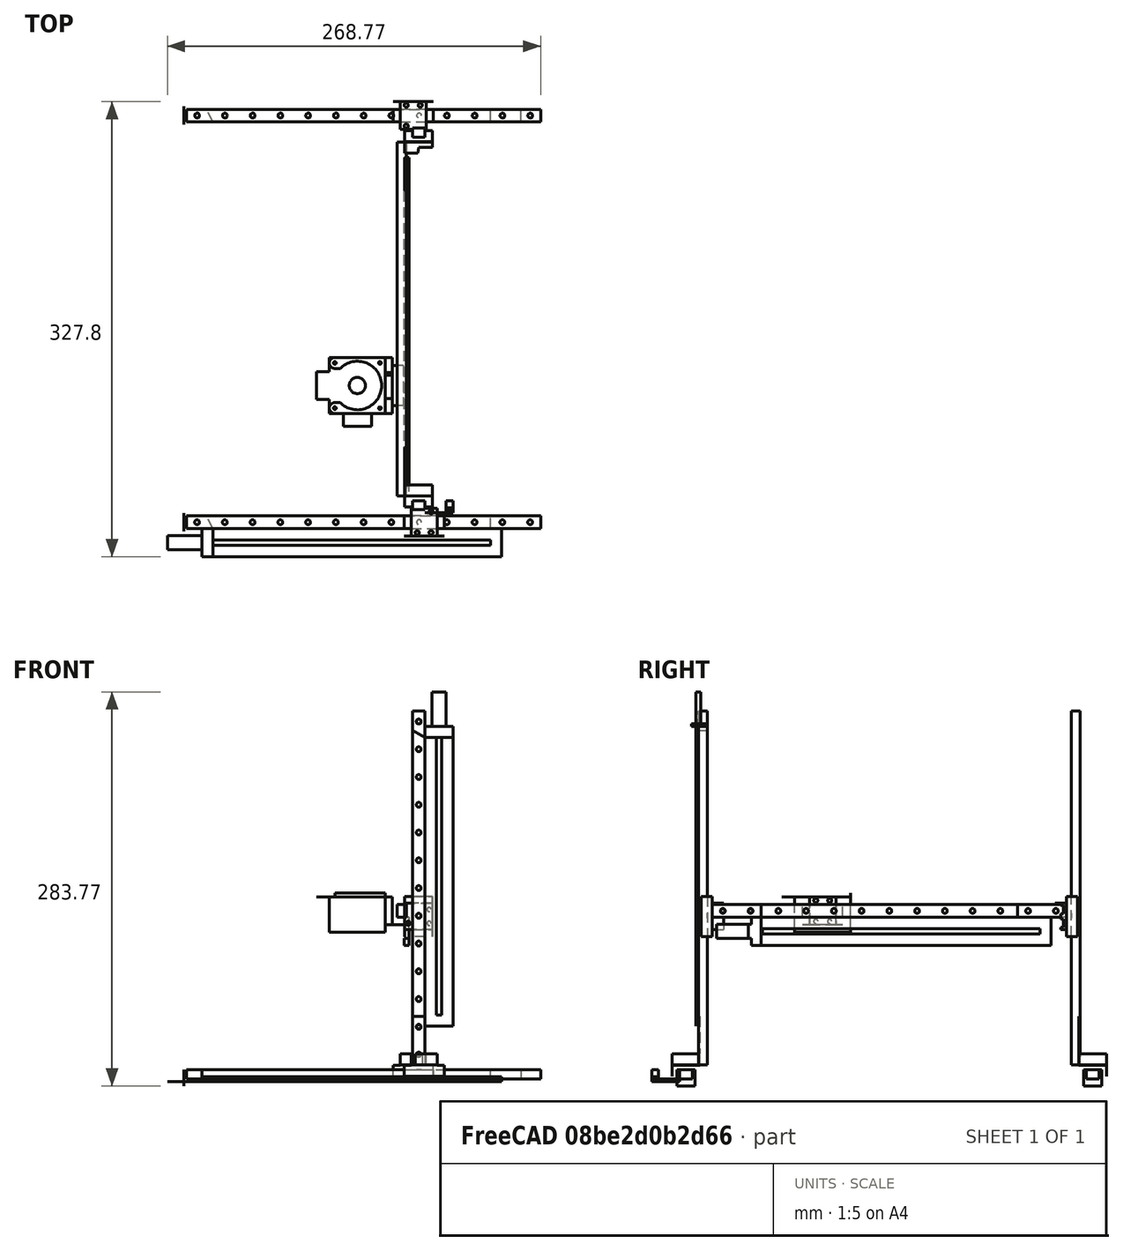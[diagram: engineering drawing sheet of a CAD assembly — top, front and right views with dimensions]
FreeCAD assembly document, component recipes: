
FREECAD ASSEMBLY — COMPONENT RECIPES ("v8")

This assembly document has 24 components, labeled P0..P23 below (a component is one placed body or linked part). 13 of them carry a construction recipe — the FreeCAD feature program that regenerates the part from scratch, quoted from this document or its linked companion documents; the rest are supplied as boundary geometry only. No exploded tour is included for this assembly.
COMPONENT P0 — geometry summary ("BaseMagentoPot"; no construction recipe available for this part):
  bounding box: 33.3 x 21.0 x 11.5 mm
  tessellated surface: 792 triangles
  volume: 2699 mm^3 (33% of its bounding box)
COMPONENT P1 — geometry summary ("Rail"; no construction recipe available for this part):
  bounding box: 255.0 x 9.0 x 6.5 mm
  tessellated surface: 3,392 triangles
  volume: 14105 mm^3 (95% of its bounding box)
  symmetry: 2-fold rotationally symmetric about the x axis; 2-fold rotationally symmetric about the y axis; 2-fold rotationally symmetric about the z axis; mirror-symmetric across its x mid-plane, y mid-plane, z mid-plane
COMPONENT P2 — recipe-attached ("Slide", a linked part whose construction recipe lives in a companion FreeCAD document of the same project; that document's serialized recipe follows).
Construction recipe (the companion document, serialized — sketch geometry with constraints, then the solid features built on it; lengths are millimeters unless a unit is written):

FCSTD DOCUMENT  (FreeCAD 0.21R33668 +26 (Git))
Label: mgn9c_slide
License: All rights reserved
LicenseURL: http://en.wikipedia.org/wiki/All_rights_reserved
objects: Sketcher::SketchObject×4, PartDesign::Pocket×3, App::Link×1, PartDesign::Pad×1, PartDesign::Body×1
note: 13 computed .brp shape members not serialized (recipe doc carries the construction recipe); baked Part::Feature solids carry a one-line shape summary decoded from their .brp
EXTERNAL_REF file=Datasheet.FCStd obj=Spreadsheet

FEATURE [App::Link] Link  label="mgn9c"
  LinkedObject = -> <external Datasheet.FCStd>#Spreadsheet
FEATURE [Sketcher::SketchObject] Sketch002
  FullyConstrained = true
  MapMode = 5
  Support = -> [XY_Plane001]
  expr: Constraints[10] = <<mgn9c>>.Dim_W
  expr: Constraints[9] = <<mgn9c>>.Dim_L
  sketch-geometry (4):
    g0: LineSegment StartX=0 StartY=0 StartZ=0 EndX=28.9 EndY=0 EndZ=0
    g1: LineSegment StartX=28.9 StartY=0 StartZ=0 EndX=28.9 EndY=20 EndZ=0
    g2: LineSegment StartX=28.9 StartY=20 StartZ=0 EndX=0 EndY=20 EndZ=0
    g3: LineSegment StartX=0 StartY=20 StartZ=0 EndX=0 EndY=0 EndZ=0
  constraints (11):
    c: Coincident(g0,g1)
    c: Coincident(g1,g2)
    c: Coincident(g2,g3)
    c: Coincident(g3,g0)
    c: Horizontal(g0)
    c: Horizontal(g2)
    c: Vertical(g1)
    c: Vertical(g3)
    c: Coincident(g0,g-1)
    c: DistanceX(g2,g2) = 28.9
    c: DistanceY(g1,g1) = 20
FEATURE [PartDesign::Pad] Pad001
  Direction = (0,0,1)
  Length = 8
  Length2 = 10
  Profile = -> Sketch002
  ReferenceAxis = -> Sketch002 [N_Axis]
  Type = 0
  expr: Length = <<mgn9c>>.Dim_H - <<mgn9c>>.Dim_H1
FEATURE [Sketcher::SketchObject] Sketch003
  ExternalGeometry = -> [Pad001]
  FullyConstrained = true
  MapMode = 5
  Placement = pos=(0,0,0) rot=(0.57735,-0.57735,-0.57735;2.0944rad)
  Support = -> [Pad001]
  expr: Constraints[10] = <<mgn9c>>.Dim_Hr - <<mgn9c>>.Dim_H1
  expr: Constraints[8] = <<mgn9c>>.Dim_N
  expr: Constraints[9] = <<mgn9c>>.Dim_N
  sketch-geometry (4):
    g0: LineSegment StartX=-14.5 StartY=0 StartZ=0 EndX=-5.5 EndY=0 EndZ=0
    g1: LineSegment StartX=-5.5 StartY=0 StartZ=0 EndX=-5.5 EndY=4.5 EndZ=0
    g2: LineSegment StartX=-5.5 StartY=4.5 StartZ=0 EndX=-14.5 EndY=4.5 EndZ=0
    g3: LineSegment StartX=-14.5 StartY=4.5 StartZ=0 EndX=-14.5 EndY=0 EndZ=0
  constraints (12):
    c: Coincident(g0,g1)
    c: Coincident(g1,g2)
    c: Coincident(g2,g3)
    c: Coincident(g3,g0)
    c: Horizontal(g0)
    c: Horizontal(g2)
    c: Vertical(g1)
    c: Vertical(g3)
    c: DistanceX(g-5,g0) = 5.5
    c: DistanceX(g0,g-6) = 5.5
    c: DistanceY(g1,g1) = 4.5
    c: PointOnObject(g0,g-5)
FEATURE [PartDesign::Pocket] Pocket001
  BaseFeature = -> Pad001
  Direction = (1,0,0)
  Length = 28.9
  Length2 = 5
  Profile = -> Sketch003
  ReferenceAxis = -> Sketch003 [N_Axis]
  Type = 0
  expr: Length = <<mgn9c>>.Dim_L
FEATURE [Sketcher::SketchObject] Sketch004
  ExternalGeometry = -> [Pocket001]
  FullyConstrained = true
  MapMode = 5
  Placement = pos=(0,0,8) rot=(0,0,1;0rad)
  Support = -> [Pocket001]
  expr: Constraints[17] = 3
  expr: Constraints[18] = 3
  expr: Constraints[19] = 3
  expr: Constraints[20] = 3
  expr: Constraints[8] = <<mgn9c>>.Dim_C
  expr: Constraints[9] = <<mgn9c>>.Dim_B
  sketch-geometry (9):
    g0: LineSegment StartX=9.45 StartY=17.5 StartZ=0 EndX=19.45 EndY=17.5 EndZ=0
    g1: LineSegment StartX=19.45 StartY=17.5 StartZ=0 EndX=19.45 EndY=2.5 EndZ=0
    g2: LineSegment StartX=19.45 StartY=2.5 StartZ=0 EndX=9.45 EndY=2.5 EndZ=0
    g3: LineSegment StartX=9.45 StartY=2.5 StartZ=0 EndX=9.45 EndY=17.5 EndZ=0
    g4: GeomPoint X=14.45 Y=10 Z=0
    g5: Circle CenterX=9.45 CenterY=17.5 CenterZ=0 NormalX=0 NormalY=0 NormalZ=1 AngleXU=0 Radius=1.5
    g6: Circle CenterX=19.45 CenterY=17.5 CenterZ=0 NormalX=0 NormalY=0 NormalZ=1 AngleXU=0 Radius=1.5
    g7: Circle CenterX=19.45 CenterY=2.5 CenterZ=0 NormalX=0 NormalY=0 NormalZ=1 AngleXU=0 Radius=1.5
    g8: Circle CenterX=9.45 CenterY=2.5 CenterZ=0 NormalX=0 NormalY=0 NormalZ=1 AngleXU=0 Radius=1.5
  constraints (21):
    c: Coincident(g0,g1)
    c: Coincident(g1,g2)
    c: Coincident(g2,g3)
    c: Coincident(g3,g0)
    c: Horizontal(g0)
    c: Horizontal(g2)
    c: Vertical(g1)
    c: Vertical(g3)
    c: DistanceX(g0,g0) = 10
    c: DistanceY(g1,g1) = 15
    c: DistanceY(g-4,g2) = 2.5
    c: Symmetric(g-3,g-4,g4)
    c: Symmetric(g1,g0,g4)
    c: Coincident(g5,g0)
    c: Coincident(g6,g0)
    c: Coincident(g7,g1)
    c: Coincident(g8,g2)
    c: Diameter(g8) = 3
    c: Diameter(g7) = 3
    c: Diameter(g6) = 3
    c: Diameter(g5) = 3
FEATURE [PartDesign::Pocket] Pocket002
  BaseFeature = -> Pocket001
  Direction = (0,0,-1)
  Length = 3
  Length2 = 5
  Profile = -> Sketch004
  ReferenceAxis = -> Sketch004 [N_Axis]
  Type = 0
FEATURE [Sketcher::SketchObject] Sketch005
  ExternalGeometry = -> [Pocket002]
  FullyConstrained = true
  MapMode = 5
  Placement = pos=(0,0,8) rot=(0,0,1;0rad)
  Support = -> [Pocket002]
  expr: Constraints[19] = <<mgn9c>>.Dim_L1
  sketch-geometry (9):
    g0: LineSegment StartX=0 StartY=20 StartZ=0 EndX=5 EndY=20 EndZ=0
    g1: LineSegment StartX=5 StartY=20 StartZ=0 EndX=5 EndY=0 EndZ=0
    g2: LineSegment StartX=5 StartY=0 StartZ=0 EndX=0 EndY=0 EndZ=0
    g3: LineSegment StartX=0 StartY=0 StartZ=0 EndX=0 EndY=20 EndZ=0
    g4: LineSegment StartX=28.9 StartY=0 StartZ=0 EndX=23.9 EndY=0 EndZ=0
    g5: LineSegment StartX=23.9 StartY=0 StartZ=0 EndX=23.9 EndY=20 EndZ=0
    g6: LineSegment StartX=23.9 StartY=20 StartZ=0 EndX=28.9 EndY=20 EndZ=0
    g7: LineSegment StartX=28.9 StartY=20 StartZ=0 EndX=28.9 EndY=0 EndZ=0
    g8: GeomPoint X=14.45 Y=0 Z=0
  constraints (22):
    c: Coincident(g0,g1)
    c: Coincident(g1,g2)
    c: Coincident(g2,g3)
    c: Coincident(g3,g0)
    c: Horizontal(g0)
    c: Horizontal(g2)
    c: Vertical(g1)
    c: Vertical(g3)
    c: Coincident(g0,g-3)
    c: PointOnObject(g1,g-1)
    c: Coincident(g4,g5)
    c: Coincident(g5,g6)
    c: Coincident(g6,g7)
    c: Coincident(g7,g4)
    c: Horizontal(g6)
    c: Vertical(g5)
    c: Vertical(g7)
    c: Symmetric(g2,g-4,g8)
    c: Symmetric(g4,g1,g8)
    c: DistanceX(g1,g4) = 18.9
    c: PointOnObject(g5,g-5)
    c: Coincident(g4,g-4)
FEATURE [PartDesign::Pocket] Pocket003
  BaseFeature = -> Pocket002
  Direction = (0,0,-1)
  Length = 0.1
  Length2 = 5
  Profile = -> Sketch005
  ReferenceAxis = -> Sketch005 [N_Axis]
  Type = 0
FEATURE [PartDesign::Body] Body001  label="Slide"
  Group = -> [Sketch002,Pad001,Sketch003,Pocket001,Sketch004,Pocket002,Sketch005,Pocket003]
  Origin = -> Origin001
  Tip = -> Pocket003
COMPONENT P3 — geometry summary ("MP1_L_0200_103_5_ST"; no construction recipe available for this part):
  bounding box: 240.7 x 20.3 x 3.5 mm
  tessellated surface: 48 triangles
  volume: 13555 mm^3 (79% of its bounding box)
  symmetry: 2-fold rotationally symmetric about the x axis; mirror-symmetric across its y mid-plane, z mid-plane
COMPONENT P4 — recipe-attached ("NormalConnectorMagnet", a linked part whose construction recipe lives in a companion FreeCAD document of the same project; that document's serialized recipe follows).
Construction recipe (the companion document, serialized — sketch geometry with constraints, then the solid features built on it; lengths are millimeters unless a unit is written):

FCSTD DOCUMENT  (FreeCAD 0.21R33668 +26 (Git))
Label: NormalConnectorMagnet
License: All rights reserved
LicenseURL: http://en.wikipedia.org/wiki/All_rights_reserved
objects: Sketcher::SketchObject×26, PartDesign::Pocket×17, PartDesign::Pad×8, PartDesign::SubShapeBinder×2, PartDesign::Body×2
note: 80 computed .brp shape members not serialized (recipe doc carries the construction recipe); baked Part::Feature solids carry a one-line shape summary decoded from their .brp
EXTERNAL_REF file=MG/mgn9c_slide.FCStd obj=Body001
EXTERNAL_REF file=BaseMagnetoPot.FCStd obj=Sketch
EXTERNAL_REF file=MG/Datasheet.FCStd obj=Spreadsheet
EXTERNAL_REF file=BaseMagnetoPot.FCStd obj=Sketch001
EXTERNAL_REF file=MG/mgn9c_13.FCStd obj=Sketch

FEATURE [PartDesign::SubShapeBinder] Binder  label="Slide"
  BindCopyOnChange = 0
  BindMode = 0
  ClaimChildren = false
  Context = -> Body [Binder.]
  Fuse = false
  MakeFace = true
  OffsetFill = false
  OffsetIntersection = false
  OffsetJoinType = 0
  OffsetOpenResult = false
  PartialLoad = false
  Relative = true
  Support = -> [<external MG/mgn9c_slide.FCStd>#Body001]
  _Version = 2
FEATURE [Sketcher::SketchObject] Sketch
  ExternalGeometry = -> [Binder]
  FullyConstrained = true
  MapMode = 5
  Placement = pos=(0,0,8) rot=(0,0,1;0rad)
  Support = -> [Binder]
  expr: Constraints[5] = .Constraints.Rad
  expr: Constraints[6] = .Constraints.Rad
  sketch-geometry (7):
    g0: Circle CenterX=19.45 CenterY=17.5 CenterZ=0 NormalX=0 NormalY=0 NormalZ=1 AngleXU=0 Radius=1.5
    g1: Circle CenterX=9.45 CenterY=2.5 CenterZ=0 NormalX=0 NormalY=0 NormalZ=1 AngleXU=0 Radius=1.5
    g2: Circle CenterX=19.45 CenterY=2.5 CenterZ=0 NormalX=0 NormalY=0 NormalZ=1 AngleXU=0 Radius=1.5
    g3: LineSegment StartX=5 StartY=20 StartZ=0 EndX=23.9 EndY=20 EndZ=0
    g4: LineSegment StartX=23.9 StartY=20 StartZ=0 EndX=23.9 EndY=0 EndZ=0
    g5: LineSegment StartX=23.9 StartY=0 StartZ=0 EndX=5 EndY=0 EndZ=0
    g6: LineSegment StartX=5 StartY=0 StartZ=0 EndX=5 EndY=20 EndZ=0
  constraints (17):
    c: Coincident(g0,g-5)
    c: PointOnObject(g-4,g0)
    c: Coincident(g1,g-6)
    c: Coincident(g2,g-7)
    c: Diameter(g0) = 3  'Rad'
    c: Diameter(g1) = 3
    c: Diameter(g2) = 3
    c: Coincident(g3,g4)
    c: Coincident(g4,g5)
    c: Coincident(g5,g6)
    c: Coincident(g6,g3)
    c: Horizontal(g5)
    c: Vertical(g4)
    c: Vertical(g6)
    c: Coincident(g3,g-8)
    c: PointOnObject(g4,g-1)
    c: Coincident(g3,g-9)
FEATURE [PartDesign::Pad] Pad
  Direction = (0,0,1)
  Length = 8
  Length2 = 10
  Profile = -> Sketch
  ReferenceAxis = -> Sketch [N_Axis]
  Type = 0
FEATURE [Sketcher::SketchObject] Sketch001
  ExternalGeometry = -> [Pad,Binder]
  FullyConstrained = true
  MapMode = 5
  Placement = pos=(0,0,0) rot=(1,0,0;1.5708rad)
  Support = -> [Pad]
  sketch-geometry (4):
    g0: LineSegment StartX=5 StartY=16 StartZ=0 EndX=8 EndY=16 EndZ=0
    g1: LineSegment StartX=8 StartY=16 StartZ=0 EndX=8 EndY=0 EndZ=0
    g2: LineSegment StartX=8 StartY=0 StartZ=0 EndX=5 EndY=0 EndZ=0
    g3: LineSegment StartX=5 StartY=0 StartZ=0 EndX=5 EndY=16 EndZ=0
  constraints (11):
    c: Coincident(g0,g1)
    c: Coincident(g1,g2)
    c: Coincident(g2,g3)
    c: Coincident(g3,g0)
    c: Horizontal(g0)
    c: Horizontal(g2)
    c: Vertical(g1)
    c: Vertical(g3)
    c: Coincident(g0,g-4)
    c: PointOnObject(g2,g-5)
    c: DistanceX(g2,g1) = 3
FEATURE [PartDesign::Pad] Pad001
  BaseFeature = -> Pad
  Direction = (0,-1,2e-16)
  Length = 3
  Length2 = 10
  Profile = -> Sketch001
  ReferenceAxis = -> Sketch001 [N_Axis]
  Type = 0
FEATURE [Sketcher::SketchObject] Sketch002
  ExternalGeometry = -> [Binder,Pad001]
  FullyConstrained = true
  MapMode = 5
  Placement = pos=(0,0,0) rot=(1,0,0;3.14159rad)
  Support = -> [Pad001]
  sketch-geometry (12):
    g0: LineSegment StartX=5 StartY=0 StartZ=0 EndX=11 EndY=0 EndZ=0
    g1: LineSegment StartX=11 StartY=0 StartZ=0 EndX=11 EndY=7.65 EndZ=0
    g2: LineSegment StartX=11 StartY=7.65 StartZ=0 EndX=5 EndY=7.65 EndZ=0
    g3: LineSegment StartX=5 StartY=7.65 StartZ=0 EndX=5 EndY=0 EndZ=0
    g4: GeomPoint X=5 Y=14.8 Z=0
    g5: GeomPoint X=5 Y=-5.5 Z=0
    g6: GeomPoint X=5 Y=4.65 Z=0
    g7: Circle CenterX=8 CenterY=4.65 CenterZ=0 NormalX=0 NormalY=0 NormalZ=1 AngleXU=0 Radius=2
    g8: GeomPoint X=10 Y=4.65 Z=0
    g9: GeomPoint X=6 Y=4.65 Z=0
    g10: GeomPoint X=8 Y=6.65 Z=0
    g11: Circle CenterX=8 CenterY=4.65 CenterZ=0 NormalX=0 NormalY=0 NormalZ=1 AngleXU=0 Radius=1.5
  constraints (28):
    c: Coincident(g0,g1)
    c: Coincident(g1,g2)
    c: Coincident(g2,g3)
    c: Coincident(g3,g0)
    c: Horizontal(g0)
    c: Horizontal(g2)
    c: Vertical(g1)
    c: Vertical(g3)
    c: Coincident(g0,g-4)
    c: PointOnObject(g5,g-3)
    c: Vertical(g5,g4)
    c: Vertical(g4,g2)
    c: Symmetric(g4,g5,g6)
    c: DistanceY(g5,g4) = 20.3
    c: Horizontal(g7,g6)
    c: PointOnObject(g8,g7)
    c: PointOnObject(g9,g7)
    c: PointOnObject(g10,g7)
    c: Vertical(g10,g7)
    c: Horizontal(g9,g8)
    c: Horizontal(g7,g9)
    c: DistanceX(g8,g1) = 1
    c: DistanceY(g10,g1) = 1
    c: DistanceX(g6,g9) = 1
    c: Diameter(g7) = 4
    c: Coincident(g11,g7)
    c: Diameter(g11) = 3
    c: DistanceY(g0,g6) = 4.65  'SlideToMagnetCenter'
FEATURE [PartDesign::Pad] Pad002
  BaseFeature = -> Pad001
  Direction = (0,-2e-16,-1)
  Length = 2
  Length2 = 10
  Profile = -> Sketch002
  ReferenceAxis = -> Sketch002 [N_Axis]
  Reversed = true
  Type = 0
FEATURE [Sketcher::SketchObject] Sketch003
  ExternalGeometry = -> [Pad002]
  FullyConstrained = true
  MapMode = 5
  Placement = pos=(0,3.6e-15,16) rot=(0,0,1;0rad)
  Support = -> [Pad002]
  sketch-geometry (1):
    g0: Circle CenterX=8 CenterY=-4.65 CenterZ=0 NormalX=0 NormalY=0 NormalZ=1 AngleXU=0 Radius=2
  constraints (2):
    c: Coincident(g0,g-3)
    c: Diameter(g0) = 4  'MagnetDiameter'
FEATURE [PartDesign::Pocket] Pocket
  BaseFeature = -> Pad002
  Direction = (0,-2e-16,-1)
  Length = 15
  Length2 = 5
  Profile = -> Sketch003
  ReferenceAxis = -> Sketch003 [N_Axis]
  Type = 0
FEATURE [Sketcher::SketchObject] Sketch004
  ExternalGeometry = -> [Pocket]
  FullyConstrained = true
  MapMode = 5
  Placement = pos=(0,20,0) rot=(0,0.707107,0.707107;3.14159rad)
  Support = -> [Pocket]
  expr: Constraints[10] = <<Datasheet>>#<<mgn9c>>.Dim_P + 2 * <<Datasheet>>#<<mgn9c>>.Dim_E
  expr: Constraints[11] = <<BaseMagnetoPot>>#<<Sketch>>.Constraints.Base_End
  expr: Constraints[23] = <<Datasheet>>#<<mgn9c>>.Dim_Wr
  sketch-geometry (15):
    g0: LineSegment StartX=-5 StartY=16 StartZ=0 EndX=-16 EndY=16 EndZ=0
    g1: LineSegment StartX=-16 StartY=16 StartZ=0 EndX=-16 EndY=43 EndZ=0
    g2: LineSegment StartX=-16 StartY=43 StartZ=0 EndX=-5 EndY=43 EndZ=0
    g3: LineSegment StartX=-5 StartY=43 StartZ=0 EndX=-5 EndY=16 EndZ=0
    g4: LineSegment StartX=-35.3 StartY=36.02 StartZ=0 EndX=-16 EndY=36.02 EndZ=0
    g5: LineSegment StartX=-35.3 StartY=36.02 StartZ=0 EndX=-16 EndY=36.02 EndZ=0
    g6: LineSegment StartX=-16 StartY=36.02 StartZ=0 EndX=-16 EndY=43 EndZ=0
    g7: LineSegment StartX=-16 StartY=43 StartZ=0 EndX=-37.3 EndY=43 EndZ=0
    g8: GeomPoint X=-15 Y=16 Z=0
    g9: GeomPoint X=-6 Y=16 Z=0
    g10: GeomPoint X=-10.5 Y=16 Z=0
    g11: LineSegment StartX=-37.3 StartY=34.02 StartZ=0 EndX=-16 EndY=34.02 EndZ=0
    g12: LineSegment StartX=-16 StartY=34.02 StartZ=0 EndX=-16 EndY=16 EndZ=0
    g13: LineSegment StartX=-16 StartY=34.02 StartZ=0 EndX=-16 EndY=16 EndZ=0
    g14: LineSegment StartX=-37.3 StartY=43 StartZ=0 EndX=-37.3 EndY=34.02 EndZ=0
  constraints (37):
    c: Coincident(g0,g1)
    c: Coincident(g1,g2)
    c: Coincident(g2,g3)
    c: Coincident(g3,g0)
    c: Horizontal(g0)
    c: Horizontal(g2)
    c: Vertical(g1)
    c: Vertical(g3)
    c: Coincident(g0,g-4)
    c: Horizontal(g4)
    c: DistanceY(g-3,g2) = 35
    c: DistanceY(g-3,g4) = 28.02
    c: PointOnObject(g4,g1)
    c: Coincident(g5,g6)
    c: Coincident(g6,g7)
    c: Horizontal(g5)
    c: Horizontal(g7)
    c: Vertical(g6)
    c: Coincident(g5,g4)
    c: Coincident(g6,g2)
    c: PointOnObject(g8,g0)
    c: Symmetric(g0,g0,g10)
    c: Symmetric(g8,g9,g10)
    c: DistanceX(g8,g9) = 9
    c: DistanceX(g0,g8) = 1  'Strength'
    c: DistanceX(g5,g8) = 20.3
    c: Horizontal(g11)
    c: Coincident(g12,g11)
    c: Coincident(g12,g0)
    c: Coincident(g13,g11)
    c: PointOnObject(g11,g1)
    c: DistanceY(g11,g4) = 2
    c: Coincident(g14,g11)
    c: Vertical(g14)
    c: DistanceX(g11,g5) = 2
    c: Coincident(g7,g14)
    c: Coincident(g0,g13)
FEATURE [PartDesign::Pad] Pad003
  BaseFeature = -> Pocket
  Direction = (0,1,-2e-16)
  Length = 10
  Length2 = 10
  Profile = -> Sketch004
  ReferenceAxis = -> Sketch004 [N_Axis]
  Reversed = true
  Type = 0
  expr: Length = <<Datasheet>>#<<mgn9c>>.Dim_W / 2
FEATURE [Sketcher::SketchObject] Sketch005
  ExternalGeometry = -> [Pad003]
  FullyConstrained = true
  MapMode = 5
  Placement = pos=(4e-16,20,-5.3e-15) rot=(0,0.707107,0.707107;3.14159rad)
  Support = -> [Pad003]
  expr: Constraints[1] = <<Datasheet>>#<<mgn9c>>.Dim_P
  expr: Constraints[2] = <<Datasheet>>#<<mgn9c>>.Dim_E
  expr: Constraints[5] = 3
  sketch-geometry (3):
    g0: Circle CenterX=-10.5 CenterY=15.5 CenterZ=0 NormalX=0 NormalY=0 NormalZ=1 AngleXU=0 Radius=1.5
    g1: Circle CenterX=-10.5 CenterY=35.5 CenterZ=0 NormalX=0 NormalY=0 NormalZ=1 AngleXU=0 Radius=1.5
    g2: GeomPoint X=-10.5 Y=16 Z=0
  constraints (7):
    c: Vertical(g1,g0)
    c: DistanceY(g0,g1) = 20
    c: DistanceY(g-7,g0) = 7.5
    c: Symmetric(g-7,g-6,g2)
    c: Vertical(g2,g0)
    c: Diameter(g1) = 3
    c: Diameter(g0) = 3
FEATURE [PartDesign::Pocket] Pocket001
  BaseFeature = -> Pad003
  Direction = (0,-1,2e-16)
  Length = 10
  Length2 = 5
  Profile = -> Sketch005
  ReferenceAxis = -> Sketch005 [N_Axis]
  Type = 0
FEATURE [Sketcher::SketchObject] Sketch006
  ExternalGeometry = -> [Pocket001,Binder]
  FullyConstrained = true
  MapMode = 5
  Placement = pos=(4e-16,20,-5.3e-15) rot=(0,0.707107,0.707107;3.14159rad)
  Support = -> [Pocket001]
  expr: Constraints[11] = <<Datasheet>>#<<mgn9c>>.Dim_Wr
  sketch-geometry (5):
    g0: LineSegment StartX=-15 StartY=43 StartZ=0 EndX=-6 EndY=43 EndZ=0
    g1: LineSegment StartX=-6 StartY=43 StartZ=0 EndX=-6 EndY=8 EndZ=0
    g2: LineSegment StartX=-6 StartY=8 StartZ=0 EndX=-15 EndY=8 EndZ=0
    g3: LineSegment StartX=-15 StartY=8 StartZ=0 EndX=-15 EndY=43 EndZ=0
    g4: GeomPoint X=-10.5 Y=43 Z=0
  constraints (12):
    c: Coincident(g0,g1)
    c: Coincident(g1,g2)
    c: Coincident(g2,g3)
    c: Coincident(g3,g0)
    c: Horizontal(g0)
    c: Horizontal(g2)
    c: Vertical(g1)
    c: Vertical(g3)
    c: PointOnObject(g1,g-8)
    c: Symmetric(g-7,g-7,g4)
    c: Symmetric(g0,g0,g4)
    c: DistanceX(g0,g0) = 9
FEATURE [PartDesign::Pocket] Pocket002
  BaseFeature = -> Pocket001
  Direction = (0,-1,2e-16)
  Length = 1
  Length2 = 5
  Profile = -> Sketch006
  ReferenceAxis = -> Sketch006 [N_Axis]
  Type = 0
  expr: Length = <<Datasheet>>#<<mgn9c>>.Dim_H1 / 2
FEATURE [Sketcher::SketchObject] Sketch007
  ExternalGeometry = -> [Pocket002]
  FullyConstrained = true
  MapMode = 5
  Placement = pos=(4e-16,20,-5.3e-15) rot=(0,0.707107,0.707107;3.14159rad)
  Support = -> [Pocket002]
  sketch-geometry (10):
    g0: LineSegment StartX=-15 StartY=43 StartZ=0 EndX=-35.3 EndY=43 EndZ=0
    g1: LineSegment StartX=-35.3 StartY=43 StartZ=0 EndX=-35.3 EndY=36.02 EndZ=0
    g2: LineSegment StartX=-35.3 StartY=36.02 StartZ=0 EndX=-15 EndY=36.02 EndZ=0
    g3: LineSegment StartX=-15 StartY=36.02 StartZ=0 EndX=-15 EndY=43 EndZ=0
    g4: LineSegment StartX=-20.07 StartY=36.02 StartZ=0 EndX=-20.07 EndY=34.02 EndZ=0
    g5: LineSegment StartX=-20.07 StartY=34.02 StartZ=0 EndX=-30.23 EndY=34.02 EndZ=0
    g6: LineSegment StartX=-30.23 StartY=34.02 StartZ=0 EndX=-30.23 EndY=36.02 EndZ=0
    g7: GeomPoint X=-25.15 Y=36.02 Z=0
    g8: LineSegment StartX=-35.3 StartY=36.02 StartZ=0 EndX=-30.23 EndY=36.02 EndZ=0
    g9: LineSegment StartX=-20.07 StartY=36.02 StartZ=0 EndX=-15 EndY=36.02 EndZ=0
  constraints (25):
    c: Coincident(g0,g1)
    c: Coincident(g1,g2)
    c: Coincident(g2,g3)
    c: Coincident(g3,g0)
    c: Horizontal(g0)
    c: Horizontal(g2)
    c: Vertical(g1)
    c: Vertical(g3)
    c: Coincident(g0,g-4)
    c: DistanceY(g-6,g1) = 2
    c: DistanceX(g-6,g1) = 2
    c: Coincident(g4,g5)
    c: Coincident(g5,g6)
    c: Horizontal(g5)
    c: Vertical(g4)
    c: Vertical(g6)
    c: PointOnObject(g6,g2)
    c: PointOnObject(g4,g-5)
    c: Symmetric(g1,g3,g7)
    c: Symmetric(g6,g4,g7)
    c: DistanceX(g6,g4) = 10.16
    c: Coincident(g8,g1)
    c: Coincident(g8,g6)
    c: Coincident(g9,g4)
    c: Coincident(g9,g3)
FEATURE [PartDesign::Pocket] Pocket003
  BaseFeature = -> Pocket002
  Direction = (0,-1,2e-16)
  Length = 3
  Length2 = 5
  Profile = -> Sketch007
  ReferenceAxis = -> Sketch007 [N_Axis]
  Type = 0
FEATURE [Sketcher::SketchObject] Sketch008
  ExternalGeometry = -> [Pocket003]
  FullyConstrained = true
  MapMode = 5
  Placement = pos=(4e-16,20,-5.3e-15) rot=(0,0.707107,0.707107;3.14159rad)
  Support = -> [Pocket003]
  expr: Constraints[10] = <<BaseMagnetoPot>>#<<Sketch>>.Constraints.EndStopDistance
  sketch-geometry (4):
    g0: LineSegment StartX=-5 StartY=16 StartZ=0 EndX=-6 EndY=16 EndZ=0
    g1: LineSegment StartX=-6 StartY=16 StartZ=0 EndX=-6 EndY=22.05 EndZ=0
    g2: LineSegment StartX=-6 StartY=22.05 StartZ=0 EndX=-5 EndY=22.05 EndZ=0
    g3: LineSegment StartX=-5 StartY=22.05 StartZ=0 EndX=-5 EndY=16 EndZ=0
  constraints (12):
    c: Coincident(g0,g1)
    c: Coincident(g1,g2)
    c: Coincident(g2,g3)
    c: Coincident(g3,g0)
    c: Horizontal(g0)
    c: Horizontal(g2)
    c: Vertical(g1)
    c: Vertical(g3)
    c: Coincident(g0,g-5)
    c: PointOnObject(g1,g-4)
    c: DistanceY(g-3,g2) = 14.05
    c: DistanceY(g3,g3) = 6.05  'StopperLength'
FEATURE [PartDesign::Pad] Pad004
  BaseFeature = -> Pocket003
  Direction = (0,1,-2e-16)
  Length = 2.5
  Length2 = 10
  Profile = -> Sketch008
  ReferenceAxis = -> Sketch008 [N_Axis]
  Type = 0
FEATURE [Sketcher::SketchObject] Sketch009
  ExternalGeometry = -> [Pad004]
  FullyConstrained = true
  MapMode = 5
  Placement = pos=(5,-1e-16,0) rot=(-0.57735,0.57735,0.57735;4.18879rad)
  Support = -> [Pad004]
  sketch-geometry (3):
    g0: LineSegment StartX=-22.5 StartY=20.05 StartZ=0 EndX=-20 EndY=16 EndZ=0
    g1: LineSegment StartX=-20 StartY=16 StartZ=0 EndX=-22.5 EndY=16 EndZ=0
    g2: LineSegment StartX=-22.5 StartY=16 StartZ=0 EndX=-22.5 EndY=20.05 EndZ=0
  constraints (7):
    c: PointOnObject(g0,g-5)
    c: Coincident(g0,g-4)
    c: Coincident(g1,g0)
    c: Coincident(g1,g-5)
    c: Coincident(g2,g1)
    c: Coincident(g2,g0)
    c: DistanceY(g0,g-5) = 2  'StopperTopLength'
FEATURE [PartDesign::Pocket] Pocket004
  BaseFeature = -> Pad004
  Direction = (1,0,0)
  Length = 5
  Length2 = 5
  Profile = -> Sketch009
  ReferenceAxis = -> Sketch009 [N_Axis]
  Type = 1
FEATURE [Sketcher::SketchObject] Sketch010
  ExternalGeometry = -> [Pocket004]
  FullyConstrained = true
  MapMode = 5
  Placement = pos=(5,0,0) rot=(0.57735,-0.57735,-0.57735;2.0944rad)
  Support = -> [Pocket004]
  sketch-geometry (3):
    g0: LineSegment StartX=-10 StartY=16 StartZ=0 EndX=-16 EndY=43 EndZ=0
    g1: LineSegment StartX=-16 StartY=43 StartZ=0 EndX=-10 EndY=43 EndZ=0
    g2: LineSegment StartX=-10 StartY=43 StartZ=0 EndX=-10 EndY=16 EndZ=0
  constraints (7):
    c: Coincident(g0,g-3)
    c: PointOnObject(g0,g-4)
    c: Coincident(g1,g-4)
    c: Coincident(g2,g0)
    c: Coincident(g0,g1)
    c: DistanceX(g-4,g0) = 4
    c: Coincident(g1,g2)
FEATURE [PartDesign::Pocket] Pocket005
  BaseFeature = -> Pocket004
  Direction = (1,0,0)
  Length = 5
  Length2 = 5
  Profile = -> Sketch010
  ReferenceAxis = -> Sketch010 [N_Axis]
  Type = 1
FEATURE [PartDesign::SubShapeBinder] Binder001  label="Slide001"
  BindCopyOnChange = 0
  BindMode = 0
  ClaimChildren = false
  Context = -> Body001 [Binder001.]
  Fuse = false
  MakeFace = true
  OffsetFill = false
  OffsetIntersection = false
  OffsetJoinType = 0
  OffsetOpenResult = false
  PartialLoad = false
  Relative = true
  Support = -> [<external MG/mgn9c_slide.FCStd>#Body001]
  _Version = 2
FEATURE [Sketcher::SketchObject] Sketch011
  ExternalGeometry = -> [Binder001]
  FullyConstrained = true
  MapMode = 5
  Placement = pos=(0,0,8) rot=(0,0,1;0rad)
  Support = -> [Binder001]
  expr: Constraints[13] = .Constraints.Rad
  expr: Constraints[14] = .Constraints.Rad
  expr: Constraints[15] = .Constraints.Rad
  sketch-geometry (7):
    g0: LineSegment StartX=5 StartY=0 StartZ=0 EndX=23.9 EndY=0 EndZ=0
    g1: LineSegment StartX=23.9 StartY=0 StartZ=0 EndX=23.9 EndY=20 EndZ=0
    g2: LineSegment StartX=23.9 StartY=20 StartZ=0 EndX=5 EndY=20 EndZ=0
    g3: LineSegment StartX=5 StartY=20 StartZ=0 EndX=5 EndY=0 EndZ=0
    g4: Circle CenterX=19.45 CenterY=17.5 CenterZ=0 NormalX=0 NormalY=0 NormalZ=1 AngleXU=0 Radius=1.5
    g5: Circle CenterX=19.45 CenterY=2.5 CenterZ=0 NormalX=0 NormalY=0 NormalZ=1 AngleXU=0 Radius=1.5
    g6: Circle CenterX=9.45 CenterY=2.5 CenterZ=0 NormalX=0 NormalY=0 NormalZ=1 AngleXU=0 Radius=1.5
  constraints (17):
    c: Coincident(g0,g1)
    c: Coincident(g1,g2)
    c: Coincident(g2,g3)
    c: Coincident(g3,g0)
    c: Horizontal(g0)
    c: Horizontal(g2)
    c: Vertical(g1)
    c: Vertical(g3)
    c: Coincident(g0,g-7)
    c: Coincident(g1,g-6)
    c: Coincident(g4,g-3)
    c: Coincident(g5,g-4)
    c: Diameter(g-5) = 3  'Rad'
    c: Diameter(g6) = 3
    c: Diameter(g5) = 3
    c: Diameter(g4) = 3
    c: Coincident(g6,g-5)
FEATURE [PartDesign::Pad] Pad005
  Direction = (0,0,1)
  Length = 8
  Length2 = 10
  Profile = -> Sketch011
  ReferenceAxis = -> Sketch011 [N_Axis]
  Reversed = true
  Type = 0
FEATURE [Sketcher::SketchObject] Sketch012
  ExternalGeometry = -> [Pad005]
  FullyConstrained = true
  MapMode = 5
  Placement = pos=(0,20,0) rot=(0,0.707107,0.707107;3.14159rad)
  Support = -> [Pad005]
  expr: Constraints[10] = <<Datasheet>>#<<mgn9c>>.Dim_Wr
  expr: Constraints[11] = <<Sketch004>>.Constraints.Strength
  expr: Constraints[21] = <<BaseMagnetoPot>>#<<Sketch>>.Constraints.PartWidth
  expr: Constraints[22] = <<BaseMagnetoPot>>#<<Sketch>>.Constraints.Rail_To_Part
  expr: Constraints[23] = <<BaseMagnetoPot>>#<<Sketch>>.Constraints.PartStartToActiveStart
  expr: Constraints[30] = <<Datasheet>>#<<mgn9c>>.Dim_P
  expr: Constraints[31] = <<Datasheet>>#<<mgn9c>>.Dim_E
  expr: Constraints[32] = <<Datasheet>>#<<mgn9c>>.Dim_d
  expr: Constraints[33] = <<Datasheet>>#<<mgn9c>>.Dim_E
  expr: Constraints[39] = <<Sketch004>>.Constraints.Strength
  expr: Constraints[44] = <<BaseMagnetoPot>>#<<Sketch001>>.Constraints.Strength
  expr: Constraints[45] = <<BaseMagnetoPot>>#<<Sketch001>>.Constraints.Strength
  expr: Constraints[54] = <<BaseMagnetoPot>>#<<Sketch>>.Constraints.Base_End
  expr: Constraints[9] = <<mgn9c_13>>#<<Sketch>>.Constraints.Rail_Length
  sketch-geometry (21):
    g0: LineSegment StartX=-15 StartY=8 StartZ=0 EndX=-6 EndY=8 EndZ=0
    g1: LineSegment StartX=-6 StartY=8 StartZ=0 EndX=-6 EndY=-247 EndZ=0
    g2: LineSegment StartX=-6 StartY=-247 StartZ=0 EndX=-15 EndY=-247 EndZ=0
    g3: LineSegment StartX=-15 StartY=-247 StartZ=0 EndX=-15 EndY=8 EndZ=0
    g4: LineSegment StartX=-35.3 StartY=-3.12 StartZ=0 EndX=-15 EndY=-3.12 EndZ=0
    g5: LineSegment StartX=-15 StartY=-3.12 StartZ=0 EndX=-15 EndY=-11.05 EndZ=0
    g6: LineSegment StartX=-15 StartY=-11.05 StartZ=0 EndX=-35.3 EndY=-11.05 EndZ=0
    g7: LineSegment StartX=-35.3 StartY=-11.05 StartZ=0 EndX=-35.3 EndY=-3.12 EndZ=0
    g8: LineSegment StartX=-23.9 StartY=0 StartZ=0 EndX=-5 EndY=0 EndZ=0
    g9: LineSegment StartX=-5 StartY=0 StartZ=0 EndX=-5 EndY=-27 EndZ=0
    g10: LineSegment StartX=-5 StartY=-27 StartZ=0 EndX=-16 EndY=-27 EndZ=0
    g11: Circle CenterX=-10.5 CenterY=-19.5 CenterZ=0 NormalX=0 NormalY=0 NormalZ=1 AngleXU=0 Radius=1.75
    g12: LineSegment StartX=-10.5 StartY=-19.5 StartZ=0 EndX=-10.5 EndY=0.5 EndZ=0
    g13: LineSegment StartX=-35.3 StartY=-11.05 StartZ=0 EndX=-16 EndY=-11.05 EndZ=0
    g14: LineSegment StartX=-16 StartY=-11.05 StartZ=0 EndX=-16 EndY=-27 EndZ=0
    g15: LineSegment StartX=-23.9 StartY=0 StartZ=0 EndX=-37.3 EndY=-1.12 EndZ=0
    g16: LineSegment StartX=-37.3 StartY=-1.12 StartZ=0 EndX=-37.3 EndY=-11.05 EndZ=0
    g17: GeomPoint X=-25.15 Y=-11.05 Z=0
    g18: LineSegment StartX=-37.3 StartY=-11.05 StartZ=0 EndX=-35.3 EndY=-11.05 EndZ=0
    g19: LineSegment StartX=-35.3 StartY=-11.05 StartZ=0 EndX=-16 EndY=-11.05 EndZ=0
    g20: GeomPoint X=-15 Y=-218.98 Z=0
  constraints (56):
    c: Coincident(g0,g1)
    c: Coincident(g1,g2)
    c: Coincident(g2,g3)
    c: Coincident(g3,g0)
    c: Horizontal(g0)
    c: Horizontal(g2)
    c: Vertical(g1)
    c: Vertical(g3)
    c: Horizontal(g0,g-3)
    c: DistanceY(g1,g1) = 255
    c: DistanceX(g0,g0) = 9
    c: DistanceX(g0,g-3) = 1
    c: Coincident(g4,g5)
    c: Coincident(g5,g6)
    c: Coincident(g6,g7)
    c: Coincident(g7,g4)
    c: Horizontal(g4)
    c: Horizontal(g6)
    c: Vertical(g5)
    c: Vertical(g7)
    c: PointOnObject(g5,g3)
    c: DistanceX(g4,g4) = 20.3
    c: DistanceY(g4,g0) = 11.12
    c: DistanceY(g7,g7) = 7.93
    c: Coincident(g8,g-4)
    c: Coincident(g9,g8)
    c: Vertical(g9)
    c: Coincident(g10,g9)
    c: Horizontal(g10)
    c: Coincident(g11,g12)
    c: DistanceY(g12,g12) = 20
    c: DistanceY(g9,g11) = 7.5
    c: Diameter(g11) = 3.5
    c: DistanceY(g12,g-3) = 7.5
    c: Coincident(g13,g7)
    c: PointOnObject(g13,g6)
    c: Coincident(g14,g13)
    c: Vertical(g14)
    c: Coincident(g10,g14)
    c: DistanceX(g13,g5) = 1
    c: Symmetric(g0,g0,g12)
    c: Coincident(g8,g15)
    c: Coincident(g15,g16)
    c: Vertical(g16)
    c: DistanceX(g16,g7) = 2
    c: DistanceY(g7,g15) = 2
    c: Coincident(g8,g-4)
    c: Symmetric(g7,g5,g17)
    c: Horizontal(g16,g6)
    c: Coincident(g18,g16)
    c: Coincident(g18,g6)
    c: Coincident(g19,g18)
    c: Coincident(g19,g14)
    c: PointOnObject(g20,g3)
    c: DistanceY(g2,g20) = 28.02
    c: DistanceY(g20,g4) = 215.86
FEATURE [PartDesign::Pad] Pad006
  BaseFeature = -> Pad005
  Direction = (0,1,-2e-16)
  Length = 10
  Length2 = 10
  Profile = -> Sketch012
  ReferenceAxis = -> Sketch012 [N_Axis]
  Reversed = true
  Type = 0
  expr: Length = <<Datasheet>>#<<mgn9c>>.Dim_W / 2
FEATURE [Sketcher::SketchObject] Sketch015  label="Measurements"
  ExternalGeometry = -> [Pocket005]
  FullyConstrained = true
  MapMode = 5
  Support = -> [XY_Plane]
  constraints (3):
    c: DistanceY(g-6,g-4) = 2.5  'SlideStopHeight'
    c: DistanceY(g-3,g-6) = 1  'RailGuideHeight'
    c: DistanceY(g-5,g-3) = 2  'MagnetoPotHeightIndent'
FEATURE [Sketcher::SketchObject] Sketch017
  ExternalGeometry = -> [Pad006]
  FullyConstrained = true
  MapMode = 5
  Placement = pos=(2e-16,20,-5.2e-15) rot=(0,0.707107,0.707107;3.14159rad)
  Support = -> [Pad006]
  expr: Constraints[1] = <<Datasheet>>#<<mgn9c>>.Dim_d
  expr: Constraints[2] = <<Datasheet>>#<<mgn9c>>.Dim_P
  sketch-geometry (1):
    g0: Circle CenterX=-10.5 CenterY=0.5 CenterZ=0 NormalX=0 NormalY=0 NormalZ=1 AngleXU=0 Radius=1.75
  constraints (3):
    c: Vertical(g-3,g0)
    c: Diameter(g0) = 3.5
    c: DistanceY(g-3,g0) = 20
FEATURE [PartDesign::Pocket] Pocket009
  BaseFeature = -> Pad006
  Direction = (0,-1,2e-16)
  Length = 10
  Length2 = 5
  Profile = -> Sketch017
  ReferenceAxis = -> Sketch017 [N_Axis]
  Type = 0
  expr: Length = <<Datasheet>>#<<mgn9c>>.Dim_W / 2
FEATURE [Sketcher::SketchObject] Sketch014
  ExternalGeometry = -> [Pocket009]
  FullyConstrained = true
  MapMode = 5
  Placement = pos=(2e-16,20,-5.2e-15) rot=(0,0.707107,0.707107;3.14159rad)
  Support = -> [Pocket009]
  expr: Constraints[28] = <<Datasheet>>#<<mgn9c>>.Dim_Wr
  expr: Constraints[8] = <<BaseMagnetoPot>>#<<Sketch>>.Constraints.PartWidth
  expr: Constraints[9] = <<BaseMagnetoPot>>#<<Sketch>>.Constraints.PartStartToActiveStart
  sketch-geometry (13):
    g0: LineSegment StartX=-35.3 StartY=-11.05 StartZ=0 EndX=-15 EndY=-11.05 EndZ=0
    g1: LineSegment StartX=-15 StartY=-11.05 StartZ=0 EndX=-15 EndY=-3.12 EndZ=0
    g2: LineSegment StartX=-15 StartY=-3.12 StartZ=0 EndX=-35.3 EndY=-3.12 EndZ=0
    g3: LineSegment StartX=-35.3 StartY=-3.12 StartZ=0 EndX=-35.3 EndY=-11.05 EndZ=0
    g4: LineSegment StartX=-15 StartY=-3.12 StartZ=0 EndX=-6 EndY=-3.12 EndZ=0
    g5: LineSegment StartX=-6 StartY=-3.12 StartZ=0 EndX=-6 EndY=-27 EndZ=0
    g6: LineSegment StartX=-6 StartY=-27 StartZ=0 EndX=-16 EndY=-27 EndZ=0
    g7: LineSegment StartX=-16 StartY=-11.05 StartZ=0 EndX=-16 EndY=-27 EndZ=0
    g8: LineSegment StartX=-35.3 StartY=-11.05 StartZ=0 EndX=-16 EndY=-11.05 EndZ=0
    g9: LineSegment StartX=-6 StartY=-3.12 StartZ=0 EndX=-6 EndY=8 EndZ=0
    g10: LineSegment StartX=-6 StartY=8 StartZ=0 EndX=-15 EndY=8 EndZ=0
    g11: LineSegment StartX=-15 StartY=8 StartZ=0 EndX=-15 EndY=-3.12 EndZ=0
    g12: LineSegment StartX=-10.5 StartY=0.5 StartZ=0 EndX=-10.5 EndY=-3.12 EndZ=0
  constraints (35):
    c: Coincident(g0,g1)
    c: Coincident(g1,g2)
    c: Coincident(g2,g3)
    c: Coincident(g3,g0)
    c: Horizontal(g0)
    c: Horizontal(g2)
    c: Vertical(g1)
    c: Vertical(g3)
    c: DistanceX(g2,g2) = 20.3
    c: DistanceY(g1,g1) = 7.93
    c: Coincident(g4,g2)
    c: Horizontal(g4)
    c: Coincident(g5,g4)
    c: Vertical(g5)
    c: Coincident(g6,g5)
    c: Horizontal(g6)
    c: Coincident(g7,g6)
    c: Coincident(g8,g3)
    c: Coincident(g8,g7)
    c: Coincident(g9,g10)
    c: Coincident(g10,g11)
    c: Horizontal(g10)
    c: Vertical(g9)
    c: Vertical(g11)
    c: Coincident(g4,g9)
    c: Coincident(g1,g11)
    c: PointOnObject(g10,g-4)
    c: PointOnObject(g7,g0)
    c: DistanceX(g10,g10) = 9
    c: Coincident(g12,g-6)
    c: PointOnObject(g12,g4)
    c: Symmetric(g10,g9,g12)
    c: Coincident(g6,g-7)
    c: Coincident(g-5,g7)
    c: DistanceX(g9,g-4) = 1  'SlideGuideWidth'
FEATURE [PartDesign::Pocket] Pocket010
  BaseFeature = -> Pocket009
  Direction = (0,-1,2e-16)
  Length = 1
  Length2 = 5
  Profile = -> Sketch014
  ReferenceAxis = -> Sketch014 [N_Axis]
  Type = 0
  expr: Length = <<Measurements>>.Constraints.RailGuideHeight
FEATURE [Sketcher::SketchObject] Sketch016
  ExternalGeometry = -> [Pocket010]
  FullyConstrained = true
  MapMode = 5
  Placement = pos=(-2e-16,19,-4.5e-15) rot=(0,0.707107,0.707107;3.14159rad)
  Support = -> [Pocket010]
  sketch-geometry (4):
    g0: LineSegment StartX=-35.3 StartY=-27 StartZ=0 EndX=-15 EndY=-27 EndZ=0
    g1: LineSegment StartX=-15 StartY=-27 StartZ=0 EndX=-15 EndY=-3.12 EndZ=0
    g2: LineSegment StartX=-15 StartY=-3.12 StartZ=0 EndX=-35.3 EndY=-3.12 EndZ=0
    g3: LineSegment StartX=-35.3 StartY=-3.12 StartZ=0 EndX=-35.3 EndY=-27 EndZ=0
  constraints (11):
    c: Coincident(g0,g1)
    c: Coincident(g1,g2)
    c: Coincident(g2,g3)
    c: Coincident(g3,g0)
    c: Horizontal(g0)
    c: Horizontal(g2)
    c: Vertical(g1)
    c: Vertical(g3)
    c: Coincident(g1,g-5)
    c: PointOnObject(g0,g-3)
    c: PointOnObject(g-4,g3)
FEATURE [PartDesign::Pocket] Pocket011
  BaseFeature = -> Pocket010
  Direction = (0,-1,2e-16)
  Length = 2
  Length2 = 5
  Profile = -> Sketch016
  ReferenceAxis = -> Sketch016 [N_Axis]
  Type = 0
  expr: Length = <<Measurements>>.Constraints.MagnetoPotHeightIndent
FEATURE [PartDesign::Pocket] Pocket012
  BaseFeature = -> Pocket011
  Direction = (0,0,-1)
  Length = 5
  Length2 = 5
  Profile = -> Pocket011 [Edge20]
  Type = 1
FEATURE [Sketcher::SketchObject] Sketch018
  ExternalGeometry = -> [Pocket012]
  FullyConstrained = true
  MapMode = 5
  Placement = pos=(-1e-15,-2.5e-15,-11.05) rot=(1,0,0;3.14159rad)
  Support = -> [Pocket012]
  expr: Constraints[1] = <<Datasheet>>#<<mgn9c>>.Dim_D
  expr: Constraints[3] = <<Datasheet>>#<<mgn9c>>.Dim_D
  expr: Constraints[5] = <<Datasheet>>#<<mgn9c>>.Dim_D
  sketch-geometry (18):
    g0: Circle CenterX=19.45 CenterY=-17.5 CenterZ=0 NormalX=0 NormalY=0 NormalZ=1 AngleXU=0 Radius=3
    g1: Circle CenterX=9.45 CenterY=-2.5 CenterZ=0 NormalX=0 NormalY=0 NormalZ=1 AngleXU=0 Radius=3
    g2: Circle CenterX=19.45 CenterY=-2.5 CenterZ=0 NormalX=0 NormalY=0 NormalZ=1 AngleXU=0 Radius=3
    g3: ArcOfCircle CenterX=19.45 CenterY=-17.5 CenterZ=0 NormalX=0 NormalY=0 NormalZ=1 AngleXU=0 Radius=3 StartAngle=5.24197e-06 EndAngle=3.14159
    g4: LineSegment StartX=16.45 StartY=-17.5 StartZ=0 EndX=22.45 EndY=-17.5 EndZ=0
    g5: LineSegment StartX=22.45 StartY=-17.5 StartZ=0 EndX=22.45 EndY=-20 EndZ=0
    g6: LineSegment StartX=22.45 StartY=-20 StartZ=0 EndX=16.45 EndY=-20 EndZ=0
    g7: LineSegment StartX=16.45 StartY=-20 StartZ=0 EndX=16.45 EndY=-17.5 EndZ=0
    g8: ArcOfCircle CenterX=19.45 CenterY=-2.5 CenterZ=0 NormalX=0 NormalY=0 NormalZ=1 AngleXU=0 Radius=3 StartAngle=3.1416 EndAngle=6.28318
    g9: ArcOfCircle CenterX=9.45 CenterY=-2.5 CenterZ=0 NormalX=0 NormalY=0 NormalZ=1 AngleXU=0 Radius=3 StartAngle=3.14159 EndAngle=6.28319
    g10: LineSegment StartX=6.45 StartY=-2.5 StartZ=0 EndX=12.45 EndY=-2.5 EndZ=0
    g11: LineSegment StartX=12.45 StartY=-2.5 StartZ=0 EndX=12.45 EndY=0 EndZ=0
    g12: LineSegment StartX=12.45 StartY=0 StartZ=0 EndX=6.45 EndY=0 EndZ=0
    g13: LineSegment StartX=6.45 StartY=0 StartZ=0 EndX=6.45 EndY=-2.5 EndZ=0
    g14: LineSegment StartX=16.45 StartY=-2.50002 StartZ=0 EndX=22.45 EndY=-2.50002 EndZ=0
    g15: LineSegment StartX=22.45 StartY=-2.50002 StartZ=0 EndX=22.45 EndY=0 EndZ=0
    g16: LineSegment StartX=22.45 StartY=0 StartZ=0 EndX=16.45 EndY=0 EndZ=0
    g17: LineSegment StartX=16.45 StartY=0 StartZ=0 EndX=16.45 EndY=-2.50002 EndZ=0
  constraints (48):
    c: Coincident(g0,g-3)
    c: Diameter(g0) = 6
    c: Coincident(g1,g-6)
    c: Diameter(g1) = 6
    c: Coincident(g2,g-5)
    c: Diameter(g2) = 6
    c: PointOnObject(g3,g0)
    c: Coincident(g0,g3)
    c: Coincident(g4,g5)
    c: Coincident(g5,g6)
    c: Coincident(g6,g7)
    c: Coincident(g7,g4)
    c: Horizontal(g4)
    c: Horizontal(g6)
    c: Vertical(g5)
    c: Vertical(g7)
    c: Coincident(g4,g3)
    c: Coincident(g3,g4)
    c: Tangent(g3,g5)
    c: PointOnObject(g5,g-7)
    c: Coincident(g8,g2)
    c: PointOnObject(g8,g2)
    c: Coincident(g9,g1)
    c: Coincident(g10,g11)
    c: Coincident(g11,g12)
    c: Coincident(g12,g13)
    c: Coincident(g13,g10)
    c: Horizontal(g10)
    c: Horizontal(g12)
    c: Vertical(g11)
    c: Vertical(g13)
    c: PointOnObject(g11,g-8)
    c: Coincident(g14,g15)
    c: Coincident(g15,g16)
    c: Coincident(g16,g17)
    c: Coincident(g17,g14)
    c: Horizontal(g14)
    c: Horizontal(g16)
    c: Vertical(g15)
    c: Vertical(g17)
    c: Coincident(g14,g8)
    c: PointOnObject(g15,g-8)
    c: Coincident(g8,g14)
    c: Tangent(g8,g15)
    c: Tangent(g9,g11)
    c: Coincident(g10,g9)
    c: PointOnObject(g9,g1)
    c: Coincident(g9,g10)
FEATURE [Sketcher::SketchObject] Sketch019  label="Measurement"
  ExternalGeometry = -> [Pocket012]
  FullyConstrained = true
  MapMode = 5
  Placement = pos=(0,20,0) rot=(0,0.707107,0.707107;3.14159rad)
  Support = -> [Pocket012]
  constraints (1):
    c: DistanceY(g-5,g-3) = 19.05  'Height'
FEATURE [PartDesign::Pocket] Pocket013
  BaseFeature = -> Pocket012
  Direction = (1e-16,2e-16,1)
  Length = 17.05
  Length2 = 5
  Profile = -> Sketch018
  ReferenceAxis = -> Sketch018 [N_Axis]
  Type = 0
  expr: Length = <<Measurement>>.Constraints.Height - 2 mm
FEATURE [Sketcher::SketchObject] Sketch020
  ExternalGeometry = -> [Pocket005]
  FullyConstrained = true
  MapMode = 5
  Placement = pos=(0,0,16) rot=(0,0,1;0rad)
  Support = -> [Pocket005]
  expr: Constraints[37] = <<Datasheet>>#<<mgn9c>>.Dim_D / 2
  expr: Constraints[38] = <<Datasheet>>#<<mgn9c>>.Dim_D / 2
  expr: Constraints[39] = <<Datasheet>>#<<mgn9c>>.Dim_D / 2
  sketch-geometry (15):
    g0: ArcOfCircle CenterX=19.45 CenterY=17.5 CenterZ=0 NormalX=0 NormalY=0 NormalZ=1 AngleXU=0 Radius=3 StartAngle=3.14159 EndAngle=6.28318
    g1: ArcOfCircle CenterX=19.45 CenterY=2.5 CenterZ=0 NormalX=0 NormalY=0 NormalZ=1 AngleXU=0 Radius=3 StartAngle=1.6056e-08 EndAngle=3.14159
    g2: ArcOfCircle CenterX=9.45 CenterY=2.5 CenterZ=0 NormalX=0 NormalY=0 NormalZ=1 AngleXU=0 Radius=3 StartAngle=6.28319 EndAngle=9.42478
    g3: LineSegment StartX=6.45 StartY=0 StartZ=0 EndX=12.45 EndY=0 EndZ=0
    g4: LineSegment StartX=12.45 StartY=0 StartZ=0 EndX=12.45 EndY=2.5 EndZ=0
    g5: LineSegment StartX=12.45 StartY=2.5 StartZ=0 EndX=6.45 EndY=2.5 EndZ=0
    g6: LineSegment StartX=6.45 StartY=2.5 StartZ=0 EndX=6.45 EndY=0 EndZ=0
    g7: LineSegment StartX=16.45 StartY=2.5 StartZ=0 EndX=22.45 EndY=2.5 EndZ=0
    g8: LineSegment StartX=22.45 StartY=2.5 StartZ=0 EndX=22.45 EndY=0 EndZ=0
    g9: LineSegment StartX=22.45 StartY=0 StartZ=0 EndX=16.45 EndY=0 EndZ=0
    g10: LineSegment StartX=16.45 StartY=0 StartZ=0 EndX=16.45 EndY=2.5 EndZ=0
    g11: LineSegment StartX=16.45 StartY=17.5 StartZ=0 EndX=22.45 EndY=17.5 EndZ=0
    g12: LineSegment StartX=22.45 StartY=17.5 StartZ=0 EndX=22.45 EndY=20 EndZ=0
    g13: LineSegment StartX=22.45 StartY=20 StartZ=0 EndX=16.45 EndY=20 EndZ=0
    g14: LineSegment StartX=16.45 StartY=20 StartZ=0 EndX=16.45 EndY=17.5 EndZ=0
  constraints (42):
    c: Coincident(g0,g-5)
    c: Coincident(g1,g-3)
    c: Coincident(g2,g-4)
    c: Coincident(g3,g4)
    c: Coincident(g4,g5)
    c: Coincident(g5,g6)
    c: Coincident(g6,g3)
    c: Horizontal(g3)
    c: Horizontal(g5)
    c: Vertical(g4)
    c: Vertical(g6)
    c: Coincident(g4,g2)
    c: Coincident(g2,g5)
    c: Tangent(g2,g6)
    c: Coincident(g7,g8)
    c: Coincident(g8,g9)
    c: Coincident(g9,g10)
    c: Coincident(g10,g7)
    c: Horizontal(g7)
    c: Horizontal(g9)
    c: Vertical(g8)
    c: Vertical(g10)
    c: Coincident(g7,g1)
    c: Coincident(g1,g7)
    c: Tangent(g1,g8)
    c: Coincident(g11,g12)
    c: Coincident(g12,g13)
    c: Coincident(g13,g14)
    c: Coincident(g14,g11)
    c: Horizontal(g11)
    c: Horizontal(g13)
    c: Vertical(g12)
    c: Vertical(g14)
    c: Coincident(g11,g0)
    c: PointOnObject(g12,g-6)
    c: Coincident(g11,g0)
    c: Tangent(g0,g12)
    c: Radius(g0) = 3
    c: Radius(g1) = 3
    c: Radius(g2) = 3
    c: PointOnObject(g3,g-1)
    c: PointOnObject(g9,g-1)
FEATURE [PartDesign::Pocket] Pocket014
  BaseFeature = -> Pocket005
  Direction = (0,0,-1)
  Length = 6
  Length2 = 5
  Profile = -> Sketch020
  ReferenceAxis = -> Sketch020 [N_Axis]
  Type = 0
FEATURE [Sketcher::SketchObject] Sketch021
  ExternalGeometry = -> [Pocket014]
  FullyConstrained = true
  MapMode = 5
  Placement = pos=(0,0,16) rot=(0,0,1;0rad)
  Support = -> [Pocket014]
  sketch-geometry (11):
    g0: LineSegment StartX=5 StartY=0 StartZ=0 EndX=23.9 EndY=0 EndZ=0
    g1: LineSegment StartX=23.9 StartY=0 StartZ=0 EndX=23.9 EndY=10 EndZ=0
    g2: LineSegment StartX=5 StartY=10 StartZ=0 EndX=5 EndY=0 EndZ=0
    g3: LineSegment StartX=23.9 StartY=10 StartZ=0 EndX=23.9 EndY=20 EndZ=0
    g4: LineSegment StartX=23.9 StartY=20 StartZ=0 EndX=16 EndY=20 EndZ=0
    g5: LineSegment StartX=16 StartY=20 StartZ=0 EndX=16 EndY=10 EndZ=0
    g6: LineSegment StartX=5 StartY=10 StartZ=0 EndX=16 EndY=10 EndZ=0
    g7: LineSegment StartX=5 StartY=-3 StartZ=0 EndX=8 EndY=-3 EndZ=0
    g8: LineSegment StartX=8 StartY=-3 StartZ=0 EndX=8 EndY=0 EndZ=0
    g9: LineSegment StartX=5 StartY=0 StartZ=0 EndX=5 EndY=-3 EndZ=0
    g10: LineSegment StartX=8 StartY=0 StartZ=0 EndX=23.9 EndY=0 EndZ=0
  constraints (26):
    c: Coincident(g0,g1)
    c: Coincident(g2,g0)
    c: Horizontal(g0)
    c: Vertical(g1)
    c: Vertical(g2)
    c: Coincident(g0,g-5)
    c: Coincident(g1,g-4)
    c: Coincident(g3,g4)
    c: Coincident(g4,g5)
    c: Horizontal(g4)
    c: Vertical(g5)
    c: Coincident(g3,g-3)
    c: Coincident(g1,g3)
    c: Coincident(g6,g2)
    c: Coincident(g6,g5)
    c: Horizontal(g6)
    c: Coincident(g5,g-4)
    c: Coincident(g7,g8)
    c: Coincident(g9,g7)
    c: Horizontal(g7)
    c: Vertical(g8)
    c: Coincident(g7,g-6)
    c: Coincident(g8,g-7)
    c: Coincident(g9,g2)
    c: Coincident(g10,g8)
    c: Coincident(g10,g1)
FEATURE [PartDesign::Pocket] Pocket015
  BaseFeature = -> Pocket014
  Direction = (0,0,-1)
  Length = 4
  Length2 = 5
  Profile = -> Sketch021
  ReferenceAxis = -> Sketch021 [N_Axis]
  Type = 0
FEATURE [Sketcher::SketchObject] Sketch022
  ExternalGeometry = -> [Pocket013]
  FullyConstrained = true
  MapMode = 5
  Placement = pos=(0,0,0) rot=(1,0,0;3.14159rad)
  Support = -> [Pocket013]
  sketch-geometry (4):
    g0: LineSegment StartX=5 StartY=-10 StartZ=0 EndX=23.9 EndY=-10 EndZ=0
    g1: LineSegment StartX=23.9 StartY=-10 StartZ=0 EndX=23.9 EndY=0 EndZ=0
    g2: LineSegment StartX=23.9 StartY=0 StartZ=0 EndX=5 EndY=0 EndZ=0
    g3: LineSegment StartX=5 StartY=0 StartZ=0 EndX=5 EndY=-10 EndZ=0
  constraints (10):
    c: Coincident(g0,g1)
    c: Coincident(g1,g2)
    c: Coincident(g2,g3)
    c: Coincident(g3,g0)
    c: Horizontal(g0)
    c: Horizontal(g2)
    c: Vertical(g1)
    c: Vertical(g3)
    c: Coincident(g0,g-3)
    c: Coincident(g1,g-4)
FEATURE [Sketcher::SketchObject] Sketch023
  AttachmentOffset = pos=(0,0,-10) rot=(0,0,1;0rad)
  ExternalGeometry = -> [Pocket015]
  FullyConstrained = true
  MapMode = 5
  Placement = pos=(0,9,-3.6e-15) rot=(0,0.707107,0.707107;3.14159rad)
  Support = -> [Pocket015]
  expr: Constraints[2] = <<Datasheet>>#<<mgn9c>>.Dim_D
  expr: Constraints[3] = <<Datasheet>>#<<mgn9c>>.Dim_D
  sketch-geometry (2):
    g0: Circle CenterX=-10.5 CenterY=15.5 CenterZ=0 NormalX=0 NormalY=0 NormalZ=1 AngleXU=0 Radius=3
    g1: Circle CenterX=-10.5 CenterY=35.5 CenterZ=0 NormalX=0 NormalY=0 NormalZ=1 AngleXU=0 Radius=3
  constraints (4):
    c: Coincident(g0,g-6)
    c: Coincident(g1,g-4)
    c: Diameter(g1) = 6
    c: Diameter(g0) = 6
FEATURE [PartDesign::Pocket] Pocket017
  BaseFeature = -> Pocket015
  Direction = (0,-1,2e-16)
  Length = 8
  Length2 = 5
  Profile = -> Sketch023
  ReferenceAxis = -> Sketch023 [N_Axis]
  Reversed = true
  Type = 0
  expr: Length = 10 - 2
FEATURE [PartDesign::Body] Body  label="NormalConnectorMagnet"
  Group = -> [Binder,Sketch,Pad,Sketch001,Pad001,Sketch002,Pad002,Sketch003,Pocket,Sketch004,Pad003,Sketch005,Pocket001,Sketch006,Pocket002,Sketch007,Pocket003,Sketch008,Pad004,Sketch009,Pocket004,Sketch010,Pocket005,Sketch015,Sketch020,Pocket014,Sketch021,Pocket015,Sketch023,Pocket017]
  Origin = -> Origin
  Tip = -> Pocket017
FEATURE [PartDesign::Pocket] Pocket016
  BaseFeature = -> Pocket013
  Direction = (0,0,1)
  Length = 4
  Length2 = 5
  Profile = -> Sketch022
  ReferenceAxis = -> Sketch022 [N_Axis]
  Type = 0
FEATURE [Sketcher::SketchObject] Sketch024
  ExternalGeometry = -> [Pocket016]
  FullyConstrained = true
  MapMode = 5
  Placement = pos=(5,0,0) rot=(0.57735,-0.57735,-0.57735;2.0944rad)
  Support = -> [Pocket016]
  sketch-geometry (3):
    g0: LineSegment StartX=-10 StartY=4 StartZ=0 EndX=-16 EndY=-27 EndZ=0
    g1: LineSegment StartX=-10 StartY=4 StartZ=0 EndX=-10 EndY=-27 EndZ=0
    g2: LineSegment StartX=-10 StartY=-27 StartZ=0 EndX=-16 EndY=-27 EndZ=0
  constraints (8):
    c: Coincident(g0,g-6)
    c: PointOnObject(g0,g-5)
    c: DistanceX(g-4,g0) = 1
    c: Coincident(g0,g1)
    c: Vertical(g1)
    c: Coincident(g1,g2)
    c: Coincident(g2,g0)
    c: Horizontal(g2)
FEATURE [PartDesign::Pocket] Pocket018
  BaseFeature = -> Pocket016
  Direction = (1,0,0)
  Length = 5
  Length2 = 5
  Profile = -> Sketch024
  ReferenceAxis = -> Sketch024 [N_Axis]
  Type = 1
FEATURE [Sketcher::SketchObject] Sketch025
  AttachmentOffset = pos=(0,0,-10) rot=(0,0,1;0rad)
  ExternalGeometry = -> [Pocket018]
  FullyConstrained = true
  MapMode = 5
  Placement = pos=(-1e-16,9,-2.3e-15) rot=(0,0.707107,0.707107;3.14159rad)
  Support = -> [Pocket018]
  expr: Constraints[2] = <<Datasheet>>#<<mgn9c>>.Dim_D
  expr: Constraints[3] = <<Datasheet>>#<<mgn9c>>.Dim_D
  sketch-geometry (2):
    g0: Circle CenterX=-10.5 CenterY=0.5 CenterZ=0 NormalX=0 NormalY=0 NormalZ=1 AngleXU=0 Radius=3
    g1: Circle CenterX=-10.5 CenterY=-19.5 CenterZ=0 NormalX=0 NormalY=0 NormalZ=1 AngleXU=0 Radius=3
  constraints (4):
    c: Coincident(g0,g-3)
    c: Coincident(g1,g-4)
    c: Diameter(g1) = 6
    c: Diameter(g0) = 6
FEATURE [PartDesign::Pocket] Pocket019
  BaseFeature = -> Pocket018
  Direction = (0,-1,2e-16)
  Length = 8
  Length2 = 5
  Profile = -> Sketch025
  ReferenceAxis = -> Sketch025 [N_Axis]
  Reversed = true
  Type = 0
  expr: Length = 10 - 2
FEATURE [Sketcher::SketchObject] Sketch026
  ExternalGeometry = -> [Pocket019]
  FullyConstrained = true
  MapMode = 5
  Placement = pos=(5,0,0) rot=(0.57735,-0.57735,-0.57735;2.0944rad)
  Support = -> [Pocket019]
  expr: Constraints[10] = <<Sketch008>>.Constraints.StopperLength
  expr: Constraints[11] = <<Measurements>>.Constraints.SlideStopHeight
  expr: Constraints[13] = <<Sketch009>>.Constraints.StopperTopLength
  expr: Constraints[9] = <<BaseMagnetoPot>>#<<Sketch>>.Constraints.EndStopDistance
  sketch-geometry (7):
    g0: LineSegment StartX=-20 StartY=2.7e-15 StartZ=0 EndX=-22.5 EndY=2.7e-15 EndZ=0
    g1: LineSegment StartX=-22.5 StartY=2.7e-15 StartZ=0 EndX=-22.5 EndY=-6.05 EndZ=0
    g2: LineSegment StartX=-22.5 StartY=-6.05 StartZ=0 EndX=-20 EndY=-6.05 EndZ=0
    g3: LineSegment StartX=-20 StartY=-6.05 StartZ=0 EndX=-20 EndY=2.7e-15 EndZ=0
    g4: GeomPoint X=-22.5 Y=-4.05 Z=0
    g5: LineSegment StartX=-22.5 StartY=-6.05 StartZ=0 EndX=-22.5 EndY=-4.05 EndZ=0
    g6: LineSegment StartX=-20 StartY=2.7e-15 StartZ=0 EndX=-22.5 EndY=-4.05 EndZ=0
  constraints (18):
    c: Coincident(g0,g1)
    c: Coincident(g1,g2)
    c: Coincident(g2,g3)
    c: Coincident(g3,g0)
    c: Horizontal(g0)
    c: Horizontal(g2)
    c: Vertical(g1)
    c: Vertical(g3)
    c: PointOnObject(g0,g-4)
    c: DistanceY(g2,g-3) = 14.05
    c: DistanceY(g3,g3) = 6.05
    c: DistanceX(g2,g2) = 2.5
    c: PointOnObject(g4,g1)
    c: DistanceY(g1,g4) = 2
    c: Coincident(g2,g5)
    c: Coincident(g5,g4)
    c: Coincident(g3,g6)
    c: Coincident(g6,g5)
FEATURE [PartDesign::Pad] Pad007
  BaseFeature = -> Pocket019
  Direction = (-1,0,0)
  Length = 1
  Length2 = 10
  Profile = -> Sketch026
  ReferenceAxis = -> Sketch026 [N_Axis]
  Reversed = true
  Type = 0
  expr: Length = <<Sketch014>>.Constraints.SlideGuideWidth
FEATURE [PartDesign::Body] Body001  label="NormalConnector"
  Group = -> [Binder001,Sketch011,Pad005,Sketch012,Pad006,Sketch014,Sketch016,Sketch017,Pocket009,Pocket010,Pocket011,Pocket012,Sketch018,Sketch019,Pocket013,Sketch022,Pocket016,Sketch024,Pocket018,Sketch025,Pocket019,Sketch026,Pad007]
  Origin = -> Origin001
  Tip = -> Pad007
COMPONENT P5 — geometry summary ("Rail001"; no construction recipe available for this part):
  bounding box: 255.0 x 9.0 x 6.5 mm
  tessellated surface: 3,392 triangles
  volume: 14105 mm^3 (95% of its bounding box)
  symmetry: 2-fold rotationally symmetric about the x axis; 2-fold rotationally symmetric about the y axis; 2-fold rotationally symmetric about the z axis; mirror-symmetric across its x mid-plane, y mid-plane, z mid-plane
COMPONENT P6 — geometry summary ("BaseMagentoPot001"; no construction recipe available for this part):
  bounding box: 33.3 x 21.0 x 11.5 mm
  tessellated surface: 792 triangles
  volume: 2699 mm^3 (33% of its bounding box)
COMPONENT P7 — geometry summary ("MP1_L_0200_103_5_ST001"; no construction recipe available for this part):
  bounding box: 240.7 x 20.3 x 3.5 mm
  tessellated surface: 48 triangles
  volume: 13555 mm^3 (79% of its bounding box)
  symmetry: 2-fold rotationally symmetric about the x axis; mirror-symmetric across its y mid-plane, z mid-plane
COMPONENT P8 — same part as P2; its construction recipe is shown at P2.
COMPONENT P9 — same part as P4; its construction recipe is shown at P4.
COMPONENT P10 — geometry summary ("MP1_L_0200_103_5_ST002"; no construction recipe available for this part):
  bounding box: 240.7 x 20.3 x 3.5 mm
  tessellated surface: 48 triangles
  volume: 13555 mm^3 (79% of its bounding box)
  symmetry: 2-fold rotationally symmetric about the x axis; mirror-symmetric across its y mid-plane, z mid-plane
COMPONENT P11 — geometry summary ("Rail002"; no construction recipe available for this part):
  bounding box: 255.0 x 9.0 x 6.5 mm
  tessellated surface: 3,392 triangles
  volume: 14105 mm^3 (95% of its bounding box)
  symmetry: 2-fold rotationally symmetric about the x axis; 2-fold rotationally symmetric about the y axis; 2-fold rotationally symmetric about the z axis; mirror-symmetric across its x mid-plane, y mid-plane, z mid-plane
COMPONENT P12 — recipe-attached ("BaseMagnetoPot_Opposite", a linked part whose construction recipe lives in a companion FreeCAD document of the same project; that document's serialized recipe follows).
Construction recipe (the companion document, serialized — sketch geometry with constraints, then the solid features built on it; lengths are millimeters unless a unit is written):

FCSTD DOCUMENT  (FreeCAD 0.21R33668 +26 (Git))
Label: BaseMagnetoPot
License: All rights reserved
LicenseURL: http://en.wikipedia.org/wiki/All_rights_reserved
objects: Sketcher::SketchObject×10, PartDesign::Pocket×5, PartDesign::Pad×4, PartDesign::SubShapeBinder×2, PartDesign::Body×2
note: 32 computed .brp shape members not serialized (recipe doc carries the construction recipe); baked Part::Feature solids carry a one-line shape summary decoded from their .brp
EXTERNAL_REF file=MG/Datasheet.FCStd obj=Spreadsheet
EXTERNAL_REF file=MG/mgn9c_13.FCStd obj=Body
EXTERNAL_REF file=MagnetoPot/MagnetoPot.FCStd obj=Body
EXTERNAL_REF file=MG/mgn9c_13.FCStd obj=Sketch

FEATURE [PartDesign::SubShapeBinder] Binder  label="Rail"
  BindCopyOnChange = 0
  BindMode = 0
  ClaimChildren = false
  Context = -> Body [Binder.]
  Fuse = false
  MakeFace = true
  OffsetFill = false
  OffsetIntersection = false
  OffsetJoinType = 0
  OffsetOpenResult = false
  PartialLoad = false
  Relative = true
  Support = -> [<external MG/mgn9c_13.FCStd>#Body]
  _Version = 2
FEATURE [Sketcher::SketchObject] Sketch
  ExternalGeometry = -> [Binder]
  FullyConstrained = true
  MapMode = 5
  Support = -> [XY_Plane]
  expr: .Constraints.EndStopToActiveDistance = (<<Datasheet>>#<<mgn9c>>.Dim_L - <<Datasheet>>#<<mgn9c>>.Dim_L1) / 2
  expr: .Constraints.PartWidth = 20.3
  expr: .Constraints.TravelDistance = 200 mm + <<Datasheet>>#<<mgn9c>>.Dim_L - 2 mm
  expr: Constraints[25] = <<Datasheet>>#<<mgn9c>>.Dim_L
  sketch-geometry (23):
    g0: Circle CenterX=7.5 CenterY=4.5 CenterZ=0 NormalX=0 NormalY=0 NormalZ=1 AngleXU=0 Radius=1.75
    g1: LineSegment StartX=0 StartY=0 StartZ=0 EndX=14.05 EndY=0 EndZ=0
    g2: LineSegment StartX=14.05 StartY=0 StartZ=0 EndX=14.05 EndY=9 EndZ=0
    g3: LineSegment StartX=14.05 StartY=9 StartZ=0 EndX=0 EndY=9 EndZ=0
    g4: LineSegment StartX=0 StartY=9 StartZ=0 EndX=0 EndY=0 EndZ=0
    g5: GeomPoint X=127.5 Y=9 Z=0
    g6: GeomPoint X=240.95 Y=9 Z=0
    g7: GeomPoint X=7.5 Y=6.25 Z=0
    g8: LineSegment StartX=14.05 StartY=9 StartZ=0 EndX=19.05 EndY=9 EndZ=0
    g9: LineSegment StartX=19.05 StartY=0 StartZ=0 EndX=14.05 EndY=9 EndZ=0
    g10: GeomPoint X=219.05 Y=0 Z=0
    g11: GeomPoint X=212.05 Y=9 Z=0
    g12: GeomPoint X=119.05 Y=0 Z=0
    g13: GeomPoint X=11.12 Y=0 Z=0
    g14: GeomPoint X=226.98 Y=0 Z=0
    g15: LineSegment StartX=19.05 StartY=0 StartZ=0 EndX=19.05 EndY=-20.3 EndZ=0
    g16: LineSegment StartX=11.12 StartY=-20.3 StartZ=0 EndX=19.05 EndY=-20.3 EndZ=0
    g17: LineSegment StartX=11.12 StartY=0 StartZ=0 EndX=11.12 EndY=-20.3 EndZ=0
    g18: GeomPoint X=0 Y=0 Z=0
    g19: GeomPoint X=11.12 Y=0 Z=0
    g20: GeomPoint X=0 Y=0 Z=0
    g21: GeomPoint X=11.12 Y=0 Z=0
    g22: LineSegment StartX=0 StartY=0 StartZ=0 EndX=11.12 EndY=0 EndZ=0
  constraints (49):
    c: Coincident(g0,g-5)
    c: Coincident(g1,g2)
    c: Coincident(g2,g3)
    c: Coincident(g3,g4)
    c: Coincident(g4,g1)
    c: Horizontal(g1)
    c: Horizontal(g3)
    c: Vertical(g2)
    c: Vertical(g4)
    c: Coincident(g1,g-4)
    c: PointOnObject(g2,g-3)
    c: Symmetric(g3,g-3,g5)
    c: Symmetric(g2,g6,g5)
    c: DistanceX(g2,g6) = 226.9  'TravelDistance'
    c: PointOnObject(g7,g0)
    c: PointOnObject(g7,g-5)
    c: Vertical(g7,g0)
    c: Coincident(g8,g3)
    c: PointOnObject(g8,g-3)
    c: DistanceX(g8,g8) = 5  'EndStopToActiveDistance'
    c: PointOnObject(g9,g-4)
    c: Coincident(g9,g3)
    c: PointOnObject(g10,g-4)
    c: DistanceX(g9,g10) = 200  'MagnetoPotActiveLength'
    c: PointOnObject(g11,g-3)
    c: DistanceX(g11,g6) = 28.9
    c: Symmetric(g10,g9,g12)
    c: Symmetric(g14,g13,g12)
    c: DistanceX(g13,g14) = 215.86  'MagnetoPotPartLength'
    c: Vertical(g9,g8)
    c: Coincident(g15,g9)
    c: Vertical(g15)
    c: Coincident(g16,g15)
    c: Horizontal(g16)
    c: Coincident(g17,g16)
    c: Coincident(g18,g4)
    c: Coincident(g19,g17)
    c: Vertical(g17)
    c: DistanceY(g17,g17) = 20.3  'PartWidth'
    c: Coincident(g20,g4)
    c: Coincident(g21,g17)
    c: Coincident(g22,g4)
    c: Coincident(g22,g17)
    c: PointOnObject(g17,g1)
    c: Coincident(g17,g13)
    c: DistanceX(g14,g-4) = 28.02  'Base_End'
    c: DistanceX(g3,g3) = 14.05  'EndStopDistance'
    c: DistanceX(g4,g17) = 11.12  'Rail_To_Part'
    c: DistanceX(g16,g15) = 7.93  'PartStartToActiveStart'
FEATURE [PartDesign::Pad] Pad
  Direction = (0,0,1)
  Length = 6
  Length2 = 10
  Profile = -> Sketch
  ReferenceAxis = -> Sketch [N_Axis]
  Reversed = true
  Type = 0
FEATURE [PartDesign::SubShapeBinder] Binder001  label="MagnetoPot_Binder"
  BindCopyOnChange = 0
  BindMode = 0
  ClaimChildren = false
  Context = -> Body [Binder001.]
  Fuse = false
  MakeFace = true
  OffsetFill = false
  OffsetIntersection = false
  OffsetJoinType = 0
  OffsetOpenResult = false
  PartialLoad = false
  Placement = pos=(5,-20.5,0) rot=(0,0,1;0rad)
  Relative = true
  Support = -> [<external MagnetoPot/MagnetoPot.FCStd>#Body]
  _Version = 2
FEATURE [Sketcher::SketchObject] Sketch001
  ExternalGeometry = -> [Pad]
  FullyConstrained = true
  MapMode = 5
  Placement = pos=(0,0,-6) rot=(1,0,0;3.14159rad)
  Support = -> [Pad]
  expr: .Constraints.MagnetoPotTailWidth = 10.16
  expr: Constraints[22] = .Constraints.Strength
  expr: Constraints[23] = .Constraints.Strength
  expr: Constraints[25] = .Constraints.Strength
  expr: Constraints[28] = .Constraints.Strength
  sketch-geometry (21):
    g0: LineSegment StartX=19.05 StartY=20.3 StartZ=0 EndX=19.05 EndY=22.3 EndZ=0
    g1: LineSegment StartX=19.05 StartY=22.3 StartZ=0 EndX=9.12 EndY=22.3 EndZ=0
    g2: LineSegment StartX=9.12 StartY=22.3 StartZ=0 EndX=9.12 EndY=2 EndZ=0
    g3: LineSegment StartX=9.12 StartY=2 StartZ=0 EndX=-2 EndY=2 EndZ=0
    g4: LineSegment StartX=-2 StartY=2 StartZ=0 EndX=-2 EndY=-11 EndZ=0
    g5: LineSegment StartX=-2 StartY=-11 StartZ=0 EndX=14.05 EndY=-11 EndZ=0
    g6: LineSegment StartX=14.05 StartY=-11 StartZ=0 EndX=14.05 EndY=-9 EndZ=0
    g7: LineSegment StartX=14.05 StartY=-9 StartZ=0 EndX=0 EndY=-9 EndZ=0
    g8: LineSegment StartX=0 StartY=0 StartZ=0 EndX=0 EndY=-9 EndZ=0
    g9: LineSegment StartX=0 StartY=0 StartZ=0 EndX=11.12 EndY=0 EndZ=0
    g10: LineSegment StartX=11.12 StartY=0 StartZ=0 EndX=11.12 EndY=20.3 EndZ=0
    g11: LineSegment StartX=11.12 StartY=20.3 StartZ=0 EndX=19.05 EndY=20.3 EndZ=0
    g12: GeomPoint X=11.12 Y=15.23 Z=0
    g13: GeomPoint X=11.12 Y=10.15 Z=0
    g14: GeomPoint X=11.12 Y=5.07 Z=0
    g15: LineSegment StartX=11.12 StartY=20.3 StartZ=0 EndX=11.12 EndY=15.23 EndZ=0
    g16: LineSegment StartX=11.12 StartY=15.23 StartZ=0 EndX=9.12 EndY=15.23 EndZ=0
    g17: LineSegment StartX=9.12 StartY=15.23 StartZ=0 EndX=9.12 EndY=22.3 EndZ=0
    g18: LineSegment StartX=11.12 StartY=5.07 StartZ=0 EndX=9.12 EndY=5.07 EndZ=0
    g19: LineSegment StartX=9.12 StartY=5.07 StartZ=0 EndX=9.12 EndY=2 EndZ=0
    g20: LineSegment StartX=11.12 StartY=0 StartZ=0 EndX=11.12 EndY=5.07 EndZ=0
  constraints (48):
    c: Coincident(g0,g-7)
    c: Vertical(g0)
    c: Horizontal(g1)
    c: Coincident(g2,g1)
    c: Coincident(g3,g2)
    c: Horizontal(g3)
    c: Coincident(g4,g3)
    c: Coincident(g5,g4)
    c: Coincident(g6,g5)
    c: Coincident(g6,g-5)
    c: Coincident(g7,g6)
    c: Coincident(g7,g-5)
    c: Coincident(g8,g-4)
    c: Coincident(g8,g7)
    c: Coincident(g9,g8)
    c: Coincident(g9,g-6)
    c: Coincident(g10,g9)
    c: Coincident(g10,g-7)
    c: Coincident(g11,g10)
    c: Coincident(g11,g0)
    c: Coincident(g0,g1)
    c: DistanceY(g0,g0) = 2  'Strength'
    c: DistanceX(g1,g10) = 2
    c: DistanceY(g9,g2) = 2
    c: Vertical(g2)
    c: DistanceX(g3,g8) = 2
    c: Vertical(g4)
    c: Horizontal(g5)
    c: DistanceY(g4,g7) = 2
    c: Vertical(g6)
    c: PointOnObject(g12,g10)
    c: Symmetric(g9,g11,g13)
    c: Symmetric(g12,g14,g13)
    c: DistanceY(g14,g12) = 10.16  'MagnetoPotTailWidth'
    c: Coincident(g15,g11)
    c: Coincident(g15,g12)
    c: Coincident(g16,g12)
    c: PointOnObject(g16,g2)
    c: Horizontal(g16)
    c: Coincident(g17,g16)
    c: Coincident(g17,g1)
    c: Coincident(g18,g14)
    c: PointOnObject(g18,g2)
    c: Coincident(g19,g18)
    c: Coincident(g19,g3)
    c: Coincident(g20,g9)
    c: Coincident(g20,g18)
    c: Horizontal(g18)
FEATURE [PartDesign::Pad] Pad001
  BaseFeature = -> Pad
  Direction = (0,0,-1)
  Length = 11.5
  Length2 = 10
  Profile = -> Sketch001
  ReferenceAxis = -> Sketch001 [N_Axis]
  Reversed = true
  Type = 0
FEATURE [Sketcher::SketchObject] Sketch002
  ExternalGeometry = -> [Pad001]
  FullyConstrained = true
  MapMode = 5
  Support = -> [Pad001]
  sketch-geometry (4):
    g0: LineSegment StartX=19.05 StartY=0 StartZ=0 EndX=11.12 EndY=0 EndZ=0
    g1: LineSegment StartX=11.12 StartY=0 StartZ=0 EndX=11.12 EndY=-20.3 EndZ=0
    g2: LineSegment StartX=11.12 StartY=-20.3 StartZ=0 EndX=19.05 EndY=-20.3 EndZ=0
    g3: LineSegment StartX=19.05 StartY=-20.3 StartZ=0 EndX=19.05 EndY=0 EndZ=0
  constraints (10):
    c: Coincident(g0,g1)
    c: Coincident(g1,g2)
    c: Coincident(g2,g3)
    c: Coincident(g3,g0)
    c: Horizontal(g0)
    c: Horizontal(g2)
    c: Vertical(g1)
    c: Coincident(g0,g-4)
    c: PointOnObject(g-3,g1)
    c: Coincident(g2,g-4)
FEATURE [PartDesign::Pocket] Pocket
  BaseFeature = -> Pad001
  Direction = (0,0,-1)
  Length = 2
  Length2 = 5
  Profile = -> Sketch002
  ReferenceAxis = -> Sketch002 [N_Axis]
  Type = 0
  expr: Length = 3.5 mm - <<Datasheet>>#<<mgn9c>>.Dim_H1 + 0.5 mm
FEATURE [Sketcher::SketchObject] Sketch003
  ExternalGeometry = -> [Pocket]
  FullyConstrained = true
  MapMode = 5
  Placement = pos=(0,0,-6) rot=(1,0,0;3.14159rad)
  Support = -> [Pocket]
  expr: Constraints[1] = <<Datasheet>>#<<mgn9c>>.Dim_D
  sketch-geometry (1):
    g0: Circle CenterX=7.5 CenterY=-4.5 CenterZ=0 NormalX=0 NormalY=0 NormalZ=1 AngleXU=0 Radius=3
  constraints (2):
    c: Coincident(g0,g-3)
    c: Diameter(g0) = 6
FEATURE [PartDesign::Pocket] Pocket001
  BaseFeature = -> Pocket
  Direction = (0,0,1)
  Length = 4
  Length2 = 5
  Profile = -> Sketch003
  ReferenceAxis = -> Sketch003 [N_Axis]
  Type = 0
  expr: Length = <<Pad>>.Length - (<<Datasheet>>#<<mgn9c>>.Dim_Hr - <<Datasheet>>#<<mgn9c>>.Dim_h - 1 mm)
FEATURE [Sketcher::SketchObject] Sketch004
  FullyConstrained = true
  MapMode = 5
  Support = -> [XY_Plane001]
  expr: Constraints[10] = <<mgn9c_13>>#<<Sketch>>.Constraints.Rail_Length
  expr: Constraints[28] = <<Sketch>>.Constraints.MagnetoPotActiveLength
  expr: Constraints[29] = <<Sketch>>.Constraints.MagnetoPotPartLength
  expr: Constraints[34] = <<Sketch>>.Constraints.TravelDistance
  expr: Constraints[35] = <<Sketch>>.Constraints.EndStopDistance
  expr: Constraints[37] = <<Sketch>>.Constraints.EndStopToActiveDistance
  expr: Constraints[38] = <<Sketch>>.Constraints.PartWidth
  expr: Constraints[44] = <<Datasheet>>#<<mgn9c>>.Dim_d
  expr: Constraints[45] = <<Datasheet>>#<<mgn9c>>.Dim_E
  expr: Constraints[9] = <<Datasheet>>#<<mgn9c>>.Dim_Wr
  sketch-geometry (21):
    g0: LineSegment StartX=-255 StartY=9 StartZ=0 EndX=0 EndY=9 EndZ=0
    g1: LineSegment StartX=0 StartY=9 StartZ=0 EndX=0 EndY=0 EndZ=0
    g2: LineSegment StartX=0 StartY=0 StartZ=0 EndX=-255 EndY=0 EndZ=0
    g3: LineSegment StartX=-255 StartY=0 StartZ=0 EndX=-255 EndY=9 EndZ=0
    g4: LineSegment StartX=-35.95 StartY=-20.3 StartZ=0 EndX=-35.95 EndY=9 EndZ=0
    g5: LineSegment StartX=-35.95 StartY=9 StartZ=0 EndX=0 EndY=9 EndZ=0
    g6: LineSegment StartX=0 StartY=9 StartZ=0 EndX=0 EndY=0 EndZ=0
    g7: LineSegment StartX=0 StartY=0 StartZ=0 EndX=-28.02 EndY=0 EndZ=0
    g8: LineSegment StartX=-28.02 StartY=0 StartZ=0 EndX=-28.02 EndY=-20.3 EndZ=0
    g9: LineSegment StartX=-35.95 StartY=-20.3 StartZ=0 EndX=-28.02 EndY=-20.3 EndZ=0
    g10: GeomPoint X=-135.95 Y=0 Z=0
    g11: GeomPoint X=-235.95 Y=0 Z=0
    g12: GeomPoint X=-35.95 Y=0 Z=0
    g13: GeomPoint X=-243.88 Y=0 Z=0
    g14: GeomPoint X=-28.02 Y=0 Z=0
    g15: GeomPoint X=-240.95 Y=9 Z=0
    g16: GeomPoint X=-14.05 Y=9 Z=0
    g17: GeomPoint X=-127.5 Y=9 Z=0
    g18: Circle CenterX=-7.5 CenterY=4.5 CenterZ=0 NormalX=0 NormalY=0 NormalZ=1 AngleXU=0 Radius=1.75
    g19: GeomPoint X=-7.5 Y=4.5 Z=0
    g20: LineSegment StartX=-7.5 StartY=4.5 StartZ=0 EndX=0 EndY=4.5 EndZ=0
  constraints (46):
    c: Coincident(g0,g1)
    c: Coincident(g1,g2)
    c: Coincident(g2,g3)
    c: Coincident(g3,g0)
    c: Horizontal(g0)
    c: Horizontal(g2)
    c: Vertical(g1)
    c: Vertical(g3)
    c: Coincident(g1,g-1)
    c: DistanceY(g1,g1) = 9
    c: DistanceX(g0,g0) = 255
    c: Coincident(g4,g5)
    c: Coincident(g5,g6)
    c: Horizontal(g5)
    c: Vertical(g4)
    c: Vertical(g6)
    c: PointOnObject(g4,g0)
    c: Coincident(g7,g6)
    c: PointOnObject(g7,g2)
    c: Coincident(g8,g7)
    c: Vertical(g8)
    c: Coincident(g9,g4)
    c: Coincident(g9,g8)
    c: Horizontal(g9)
    c: PointOnObject(g10,g2)
    c: PointOnObject(g11,g2)
    c: Symmetric(g14,g13,g10)
    c: Symmetric(g11,g12,g10)
    c: DistanceX(g11,g12) = 200
    c: DistanceX(g13,g14) = 215.86
    c: Coincident(g14,g7)
    c: PointOnObject(g15,g0)
    c: PointOnObject(g16,g0)
    c: Symmetric(g15,g16,g17)
    c: DistanceX(g15,g16) = 226.9
    c: DistanceX(g0,g15) = 14.05
    c: PointOnObject(g12,g4)
    c: DistanceX(g15,g11) = 5
    c: DistanceY(g8,g8) = 20.3
    c: Coincident(g6,g1)
    c: Coincident(g19,g18)
    c: Horizontal(g20)
    c: Coincident(g18,g20)
    c: Symmetric(g5,g6,g20)
    c: Diameter(g18) = 3.5
    c: DistanceX(g18,g20) = 7.5
FEATURE [PartDesign::Pad] Pad002
  Direction = (0,0,1)
  Length = 6
  Length2 = 10
  Profile = -> Sketch004
  ReferenceAxis = -> Sketch004 [N_Axis]
  Reversed = true
  Type = 0
  expr: Length = <<Pad>>.Length
FEATURE [Sketcher::SketchObject] Sketch006
  ExternalGeometry = -> [Pad002]
  FullyConstrained = true
  MapMode = 5
  Placement = pos=(0,0,-6) rot=(1,0,0;3.14159rad)
  Support = -> [Pad002]
  expr: Constraints[18] = <<Sketch001>>.Constraints.Strength
  expr: Constraints[19] = <<Sketch001>>.Constraints.Strength
  expr: Constraints[20] = <<Sketch001>>.Constraints.Strength
  expr: Constraints[21] = <<Sketch001>>.Constraints.Strength
  expr: Constraints[23] = <<Sketch001>>.Constraints.Strength
  expr: Constraints[27] = <<Sketch001>>.Constraints.MagnetoPotTailWidth
  sketch-geometry (17):
    g0: LineSegment StartX=2 StartY=2 StartZ=0 EndX=2 EndY=-11 EndZ=0
    g1: LineSegment StartX=2 StartY=-11 StartZ=0 EndX=-35.95 EndY=-11 EndZ=0
    g2: LineSegment StartX=-35.95 StartY=-11 StartZ=0 EndX=-35.95 EndY=-9 EndZ=0
    g3: LineSegment StartX=-35.95 StartY=22.3 StartZ=0 EndX=-26.02 EndY=22.3 EndZ=0
    g4: LineSegment StartX=-26.02 StartY=22.3 StartZ=0 EndX=-26.02 EndY=15.23 EndZ=0
    g5: LineSegment StartX=-26.02 StartY=15.23 StartZ=0 EndX=-28.02 EndY=15.23 EndZ=0
    g6: LineSegment StartX=-28.02 StartY=5.07 StartZ=0 EndX=-26.02 EndY=5.07 EndZ=0
    g7: LineSegment StartX=-26.02 StartY=5.07 StartZ=0 EndX=-26.02 EndY=2 EndZ=0
    g8: LineSegment StartX=-26.02 StartY=2 StartZ=0 EndX=2 EndY=2 EndZ=0
    g9: LineSegment StartX=-35.95 StartY=22.3 StartZ=0 EndX=-35.95 EndY=20.3 EndZ=0
    g10: GeomPoint X=-28.02 Y=10.15 Z=0
    g11: LineSegment StartX=-35.95 StartY=20.3 StartZ=0 EndX=-28.02 EndY=20.3 EndZ=0
    g12: LineSegment StartX=-28.02 StartY=20.3 StartZ=0 EndX=-28.02 EndY=15.23 EndZ=0
    g13: LineSegment StartX=-28.02 StartY=5.07 StartZ=0 EndX=-28.02 EndY=0 EndZ=0
    g14: LineSegment StartX=-28.02 StartY=0 StartZ=0 EndX=0 EndY=0 EndZ=0
    g15: LineSegment StartX=0 StartY=0 StartZ=0 EndX=0 EndY=-9 EndZ=0
    g16: LineSegment StartX=0 StartY=-9 StartZ=0 EndX=-35.95 EndY=-9 EndZ=0
  constraints (42):
    c: Vertical(g0)
    c: Coincident(g1,g0)
    c: Horizontal(g1)
    c: Coincident(g2,g1)
    c: Coincident(g2,g-6)
    c: Vertical(g2)
    c: Horizontal(g3)
    c: Coincident(g4,g3)
    c: Vertical(g4)
    c: PointOnObject(g5,g-3)
    c: Horizontal(g5)
    c: Coincident(g8,g7)
    c: Coincident(g8,g0)
    c: Horizontal(g8)
    c: Coincident(g4,g5)
    c: Coincident(g6,g7)
    c: Horizontal(g6)
    c: Vertical(g7)
    c: DistanceY(g2,g2) = 2
    c: DistanceX(g-6,g0) = 2
    c: DistanceY(g-1,g0) = 2
    c: DistanceX(g-3,g7) = 2
    c: Vertical(g4,g6)
    c: DistanceY(g-5,g3) = 2
    c: Coincident(g9,g3)
    c: Vertical(g9)
    c: Coincident(g9,g-5)
    c: DistanceY(g6,g4) = 10.16
    c: Symmetric(g-5,g-3,g10)
    c: Symmetric(g5,g6,g10)
    c: Coincident(g11,g9)
    c: Coincident(g11,g-5)
    c: Coincident(g12,g11)
    c: Coincident(g12,g5)
    c: Coincident(g6,g13)
    c: Coincident(g13,g-3)
    c: Coincident(g13,g14)
    c: Coincident(g14,g-1)
    c: Coincident(g14,g15)
    c: Coincident(g15,g-6)
    c: Coincident(g15,g16)
    c: Coincident(g16,g2)
FEATURE [Sketcher::SketchObject] Sketch007  label="Measurements"
  ExternalGeometry = -> [Pocket001]
  FullyConstrained = true
  MapMode = 5
  Placement = pos=(0,0,0) rot=(1,0,0;1.5708rad)
  Support = -> [XZ_Plane]
  constraints (3):
    c: DistanceY(g-4,g-5) = 6  'BaseHeight'
    c: DistanceY(g-4,g-6) = 4  'MagnetoPotHeight'
    c: DistanceY(g-4,g-3) = 11.5  'TotalHeight'
FEATURE [PartDesign::Body] Body  label="BaseMagentoPot"
  Group = -> [Sketch,Binder,Pad,Binder001,Sketch001,Pad001,Sketch002,Pocket,Sketch003,Pocket001,Sketch007]
  Origin = -> Origin
  Tip = -> Pocket001
FEATURE [PartDesign::Pad] Pad003
  BaseFeature = -> Pad002
  Direction = (0,0,-1)
  Length = 11.5
  Length2 = 10
  Profile = -> Sketch006
  ReferenceAxis = -> Sketch006 [N_Axis]
  Reversed = true
  Type = 0
  expr: Length = Sketch007.Constraints.TotalHeight
FEATURE [Sketcher::SketchObject] Sketch008
  ExternalGeometry = -> [Pad003]
  FullyConstrained = true
  MapMode = 5
  Support = -> [Pad003]
  sketch-geometry (4):
    g0: LineSegment StartX=-35.95 StartY=-20.3 StartZ=0 EndX=-28.02 EndY=-20.3 EndZ=0
    g1: LineSegment StartX=-28.02 StartY=-20.3 StartZ=0 EndX=-28.02 EndY=0 EndZ=0
    g2: LineSegment StartX=-28.02 StartY=0 StartZ=0 EndX=-35.95 EndY=0 EndZ=0
    g3: LineSegment StartX=-35.95 StartY=0 StartZ=0 EndX=-35.95 EndY=-20.3 EndZ=0
  constraints (10):
    c: Coincident(g0,g1)
    c: Coincident(g1,g2)
    c: Coincident(g2,g3)
    c: Coincident(g3,g0)
    c: Horizontal(g0)
    c: Horizontal(g2)
    c: Vertical(g1)
    c: Vertical(g3)
    c: Coincident(g0,g-4)
    c: Coincident(g1,g-3)
FEATURE [PartDesign::Pocket] Pocket002
  BaseFeature = -> Pad003
  Direction = (0,0,-1)
  Length = 2
  Length2 = 5
  Profile = -> Sketch008
  ReferenceAxis = -> Sketch008 [N_Axis]
  Type = 0
  expr: Length = <<Measurements>>.Constraints.BaseHeight - <<Measurements>>.Constraints.MagnetoPotHeight
FEATURE [Sketcher::SketchObject] Sketch009
  ExternalGeometry = -> [Pocket002]
  FullyConstrained = true
  MapMode = 5
  Placement = pos=(0,0,5.5) rot=(0,0,1;0rad)
  Support = -> [Pocket002]
  expr: Constraints[10] = <<Sketch>>.Constraints.EndStopDistance
  expr: Constraints[11] = <<Datasheet>>#<<mgn9c>>.Dim_W
  sketch-geometry (5):
    g0: LineSegment StartX=-35.95 StartY=14.5 StartZ=0 EndX=-14.05 EndY=14.5 EndZ=0
    g1: LineSegment StartX=-14.05 StartY=14.5 StartZ=0 EndX=-14.05 EndY=-5.5 EndZ=0
    g2: LineSegment StartX=-14.05 StartY=-5.5 StartZ=0 EndX=-35.95 EndY=-5.5 EndZ=0
    g3: LineSegment StartX=-35.95 StartY=-5.5 StartZ=0 EndX=-35.95 EndY=14.5 EndZ=0
    g4: LineSegment StartX=-7.5 StartY=4.5 StartZ=0 EndX=-35.95 EndY=4.5 EndZ=0
  constraints (14):
    c: Coincident(g0,g1)
    c: Coincident(g1,g2)
    c: Coincident(g2,g3)
    c: Coincident(g3,g0)
    c: Horizontal(g0)
    c: Horizontal(g2)
    c: Vertical(g1)
    c: Vertical(g3)
    c: Coincident(g4,g-5)
    c: PointOnObject(g4,g3)
    c: DistanceX(g0,g-6) = 14.05
    c: DistanceY(g3,g3) = 20
    c: Symmetric(g0,g2,g4)
    c: PointOnObject(g-6,g3)
FEATURE [PartDesign::Pocket] Pocket003
  BaseFeature = -> Pocket002
  Direction = (0,0,-1)
  Length = 5
  Length2 = 5
  Profile = -> Sketch009
  ReferenceAxis = -> Sketch009 [N_Axis]
  Type = 2
FEATURE [Sketcher::SketchObject] Sketch010
  ExternalGeometry = -> [Pocket003]
  FullyConstrained = true
  MapMode = 5
  Placement = pos=(0,0,-6) rot=(1,0,0;3.14159rad)
  Support = -> [Pocket003]
  expr: Constraints[1] = <<Datasheet>>#<<mgn9c>>.Dim_D
  sketch-geometry (1):
    g0: Circle CenterX=-7.5 CenterY=-4.5 CenterZ=0 NormalX=0 NormalY=0 NormalZ=1 AngleXU=0 Radius=3
  constraints (2):
    c: Coincident(g0,g-3)
    c: Diameter(g0) = 6
FEATURE [PartDesign::Pocket] Pocket004
  BaseFeature = -> Pocket003
  Direction = (0,0,1)
  Length = 4
  Length2 = 5
  Profile = -> Sketch010
  ReferenceAxis = -> Sketch010 [N_Axis]
  Type = 0
  expr: Length = <<Pad002>>.Length - (<<Datasheet>>#<<mgn9c>>.Dim_Hr - <<Datasheet>>#<<mgn9c>>.Dim_h - 1 mm)
FEATURE [PartDesign::Body] Body001  label="BaseMagnetoPot_Opposite"
  Group = -> [Sketch004,Pad002,Sketch006,Pad003,Sketch008,Pocket002,Sketch009,Pocket003,Sketch010,Pocket004]
  Origin = -> Origin001
  Placement = pos=(-11,0,0) rot=(0,0,1;0rad)
  Tip = -> Pocket004
COMPONENT P13 — same part as P2; its construction recipe is shown at P2.
COMPONENT P14 — geometry summary ("Rail003"; no construction recipe available for this part):
  bounding box: 255.0 x 9.0 x 6.5 mm
  tessellated surface: 3,392 triangles
  volume: 14105 mm^3 (95% of its bounding box)
  symmetry: 2-fold rotationally symmetric about the x axis; 2-fold rotationally symmetric about the y axis; 2-fold rotationally symmetric about the z axis; mirror-symmetric across its x mid-plane, y mid-plane, z mid-plane
COMPONENT P15 — same part as P4; its construction recipe is shown at P4.
COMPONENT P16 — same part as P2; its construction recipe is shown at P2.
COMPONENT P17 — geometry summary ("Rail004"; no construction recipe available for this part):
  bounding box: 255.0 x 9.0 x 6.5 mm
  tessellated surface: 3,392 triangles
  volume: 14105 mm^3 (95% of its bounding box)
  symmetry: 2-fold rotationally symmetric about the x axis; 2-fold rotationally symmetric about the y axis; 2-fold rotationally symmetric about the z axis; mirror-symmetric across its x mid-plane, y mid-plane, z mid-plane
COMPONENT P18 — same part as P12; its construction recipe is shown at P12.
COMPONENT P19 — geometry summary ("BaseMagentoPot002"; no construction recipe available for this part):
  bounding box: 33.3 x 21.0 x 11.5 mm
  tessellated surface: 792 triangles
  volume: 2699 mm^3 (33% of its bounding box)
COMPONENT P20 — same part as P4; its construction recipe is shown at P4.
COMPONENT P21 — same part as P2; its construction recipe is shown at P2.
COMPONENT P22 — recipe-attached ("JoystickHolder", a linked part whose construction recipe lives in a companion FreeCAD document of the same project; that document's serialized recipe follows).
Construction recipe (the companion document, serialized — sketch geometry with constraints, then the solid features built on it; lengths are millimeters unless a unit is written):

FCSTD DOCUMENT  (FreeCAD 0.21R33668 +26 (Git))
Label: Joystick_Holder
License: All rights reserved
LicenseURL: http://en.wikipedia.org/wiki/All_rights_reserved
objects: Sketcher::SketchObject×6, PartDesign::Pad×4, PartDesign::SubShapeBinder×2, PartDesign::Pocket×2, PartDesign::Body×1
note: 21 computed .brp shape members not serialized (recipe doc carries the construction recipe); baked Part::Feature solids carry a one-line shape summary decoded from their .brp
EXTERNAL_REF file=MG/mgn9c_slide.FCStd obj=Body001
EXTERNAL_REF file=R202.FCStd obj=Revolution
EXTERNAL_REF file=MG/Datasheet.FCStd obj=Spreadsheet
EXTERNAL_REF file=NormalConnectorMagnet.FCStd obj=Sketch002
EXTERNAL_REF file=NormalConnectorMagnet.FCStd obj=Pad002
EXTERNAL_REF file=NormalConnectorMagnet.FCStd obj=Sketch003

FEATURE [PartDesign::SubShapeBinder] Binder  label="Slide"
  BindCopyOnChange = 0
  BindMode = 0
  ClaimChildren = false
  Context = -> Body [Binder.]
  Fuse = false
  MakeFace = true
  OffsetFill = false
  OffsetIntersection = false
  OffsetJoinType = 0
  OffsetOpenResult = false
  PartialLoad = false
  Placement = pos=(0,0,0) rot=(0,0,1;1.5708rad)
  Relative = true
  Support = -> [<external MG/mgn9c_slide.FCStd>#Body001]
  _Version = 2
FEATURE [PartDesign::SubShapeBinder] Binder001  label="Joystick"
  BindCopyOnChange = 0
  BindMode = 0
  ClaimChildren = false
  Context = -> Body [Binder001.]
  Fuse = false
  MakeFace = true
  OffsetFill = false
  OffsetIntersection = false
  OffsetJoinType = 0
  OffsetOpenResult = false
  PartialLoad = false
  Placement = pos=(-16.5,16.5,-29.5) rot=(0,0,-1;1.5708rad)
  Relative = true
  Support = -> [<external R202.FCStd>#Revolution]
  _Version = 2
FEATURE [Sketcher::SketchObject] Sketch
  ExternalGeometry = -> [Binder001]
  FullyConstrained = true
  MapMode = 5
  Placement = pos=(-16.5,16.5,0) rot=(0,0,-1;1.5708rad)
  Support = -> [Binder001]
  sketch-geometry (17):
    g0: LineSegment StartX=-20.2 StartY=25.2 StartZ=0 EndX=20.2 EndY=25.2 EndZ=0
    g1: LineSegment StartX=20.2 StartY=25.2 StartZ=0 EndX=20.2 EndY=20.2 EndZ=0
    g2: LineSegment StartX=20.2 StartY=20.2 StartZ=0 EndX=-20.2 EndY=20.2 EndZ=0
    g3: LineSegment StartX=-20.2 StartY=20.2 StartZ=0 EndX=-20.2 EndY=25.2 EndZ=0
    g4: LineSegment StartX=-20.2 StartY=20.2 StartZ=0 EndX=-20.2 EndY=-16.25 EndZ=0
    g5: LineSegment StartX=-12.3 StartY=-16.25 StartZ=0 EndX=-12.3 EndY=-12.4483 EndZ=0
    g6: ArcOfCircle CenterX=-16.25 CenterY=-16.25 CenterZ=0 NormalX=0 NormalY=0 NormalZ=1 AngleXU=0 Radius=3.95 StartAngle=3.14159 EndAngle=6.28319
    g7: ArcOfCircle CenterX=0 CenterY=-1.78e-14 CenterZ=0 NormalX=0 NormalY=0 NormalZ=1 AngleXU=0 Radius=17.5 StartAngle=5.4918 EndAngle=10.2162
    g8: LineSegment StartX=12.3 StartY=-12.4483 StartZ=0 EndX=12.3 EndY=-16.25 EndZ=0
    g9: ArcOfCircle CenterX=16.25 CenterY=-16.25 CenterZ=0 NormalX=0 NormalY=0 NormalZ=1 AngleXU=0 Radius=3.95 StartAngle=3.14159 EndAngle=6.28319
    g10: LineSegment StartX=20.2 StartY=20.2 StartZ=0 EndX=20.2 EndY=-16.25 EndZ=0
    g11: Circle CenterX=-16.25 CenterY=16.25 CenterZ=0 NormalX=0 NormalY=0 NormalZ=1 AngleXU=0 Radius=1
    g12: Circle CenterX=16.25 CenterY=16.25 CenterZ=0 NormalX=0 NormalY=0 NormalZ=1 AngleXU=0 Radius=1
    g13: Circle CenterX=16.25 CenterY=-16.25 CenterZ=0 NormalX=0 NormalY=0 NormalZ=1 AngleXU=0 Radius=1
    g14: Circle CenterX=-16.25 CenterY=-16.25 CenterZ=0 NormalX=0 NormalY=0 NormalZ=1 AngleXU=0 Radius=1
    g15: GeomPoint X=-16.25 Y=-17.25 Z=0
    g16: GeomPoint X=16.25 Y=-15.25 Z=0
  constraints (39):
    c: Coincident(g0,g1)
    c: Coincident(g1,g2)
    c: Coincident(g2,g3)
    c: Coincident(g3,g0)
    c: Horizontal(g0)
    c: Vertical(g1)
    c: Vertical(g3)
    c: Coincident(g1,g-8)
    c: Coincident(g2,g-8)
    c: DistanceY(g3,g3) = 5  'Strength'
    c: Coincident(g4,g3)
    c: Vertical(g4)
    c: PointOnObject(g5,g-9)
    c: Vertical(g5)
    c: Coincident(g6,g-5)
    c: Coincident(g6,g4)
    c: Horizontal(g4,g6)
    c: Tangent(g6,g5) = -1.5708
    c: Coincident(g7,g-9)
    c: Coincident(g7,g5)
    c: Coincident(g8,g7)
    c: Coincident(g9,g-6)
    c: Tangent(g9,g-7) = 1.5708
    c: Tangent(g9,g8) = -1.5708
    c: Horizontal(g8,g9)
    c: Coincident(g10,g1)
    c: Coincident(g10,g9)
    c: Coincident(g11,g-4)
    c: Tangent(g11,g-4)
    c: Coincident(g12,g-3)
    c: Tangent(g12,g-3)
    c: Coincident(g13,g9)
    c: Coincident(g14,g6)
    c: PointOnObject(g15,g-5)
    c: PointOnObject(g15,g14)
    c: PointOnObject(g16,g-6)
    c: PointOnObject(g16,g13)
    c: Vertical(g15,g6)
    c: Vertical(g16,g9)
FEATURE [PartDesign::Pad] Pad
  Direction = (0,0,1)
  Length = 3
  Length2 = 10
  Placement = pos=(-16.5,16.5,-29.5) rot=(0,0,-1;1.5708rad)
  Profile = -> Sketch
  ReferenceAxis = -> Sketch [N_Axis]
  Type = 0
FEATURE [Sketcher::SketchObject] Sketch001
  ExternalGeometry = -> [Pad]
  FullyConstrained = true
  MapMode = 5
  Placement = pos=(8.7,16.5,-29.5) rot=(0.57735,0.57735,0.57735;2.0944rad)
  Support = -> [Pad]
  expr: .Constraints.Rad = 3
  expr: Constraints[25] = .Constraints.Rad
  expr: Constraints[26] = .Constraints.Rad
  expr: Constraints[27] = .Constraints.Rad
  expr: Constraints[30] = <<Datasheet>>#<<mgn9c>>.Dim_C
  expr: Constraints[31] = <<Datasheet>>#<<mgn9c>>.Dim_B
  expr: Constraints[8] = <<Datasheet>>#<<mgn9c>>.Dim_L1
  expr: Constraints[9] = <<Datasheet>>#<<mgn9c>>.Dim_W
  sketch-geometry (14):
    g0: LineSegment StartX=-9.45 StartY=9.5 StartZ=0 EndX=9.45 EndY=9.5 EndZ=0
    g1: LineSegment StartX=9.45 StartY=9.5 StartZ=0 EndX=9.45 EndY=29.5 EndZ=0
    g2: LineSegment StartX=9.45 StartY=29.5 StartZ=0 EndX=-9.45 EndY=29.5 EndZ=0
    g3: LineSegment StartX=-9.45 StartY=29.5 StartZ=0 EndX=-9.45 EndY=9.5 EndZ=0
    g4: GeomPoint X=1.9e-15 Y=29.5 Z=0
    g5: Circle CenterX=-5 CenterY=27 CenterZ=0 NormalX=0 NormalY=0 NormalZ=1 AngleXU=0 Radius=1.5
    g6: Circle CenterX=5 CenterY=27 CenterZ=0 NormalX=0 NormalY=0 NormalZ=1 AngleXU=0 Radius=1.5
    g7: Circle CenterX=-5 CenterY=12 CenterZ=0 NormalX=0 NormalY=0 NormalZ=1 AngleXU=0 Radius=1.5
    g8: Circle CenterX=5 CenterY=12 CenterZ=0 NormalX=0 NormalY=0 NormalZ=1 AngleXU=0 Radius=1.5
    g9: LineSegment StartX=-5 StartY=12 StartZ=0 EndX=5 EndY=12 EndZ=0
    g10: LineSegment StartX=5 StartY=12 StartZ=0 EndX=5 EndY=27 EndZ=0
    g11: LineSegment StartX=5 StartY=27 StartZ=0 EndX=-5 EndY=27 EndZ=0
    g12: LineSegment StartX=-5 StartY=27 StartZ=0 EndX=-5 EndY=12 EndZ=0
    g13: GeomPoint X=1.8e-15 Y=19.5 Z=0
  constraints (32):
    c: Coincident(g0,g1)
    c: Coincident(g1,g2)
    c: Coincident(g2,g3)
    c: Coincident(g3,g0)
    c: Horizontal(g0)
    c: Horizontal(g2)
    c: Vertical(g1)
    c: Vertical(g3)
    c: DistanceX(g2,g2) = 18.9
    c: DistanceY(g1,g1) = 20
    c: Symmetric(g-3,g-4,g4)
    c: Symmetric(g2,g1,g4)
    c: Coincident(g9,g10)
    c: Coincident(g10,g11)
    c: Coincident(g11,g12)
    c: Coincident(g12,g9)
    c: Horizontal(g9)
    c: Horizontal(g11)
    c: Vertical(g10)
    c: Vertical(g12)
    c: Coincident(g9,g7)
    c: Coincident(g10,g6)
    c: Coincident(g5,g11)
    c: Coincident(g8,g9)
    c: Diameter(g7) = 3  'Rad'
    c: Diameter(g8) = 3
    c: Diameter(g6) = 3
    c: Diameter(g5) = 3
    c: Symmetric(g1,g0,g13)
    c: Symmetric(g7,g6,g13)
    c: DistanceX(g11,g11) = 10
    c: DistanceY(g10,g10) = 15
FEATURE [PartDesign::Pad] Pad001
  BaseFeature = -> Pad
  Direction = (1,4e-16,0)
  Length = 5
  Length2 = 10
  Placement = pos=(-16.5,16.5,-29.5) rot=(0,0,-1;1.5708rad)
  Profile = -> Sketch001
  ReferenceAxis = -> Sketch001 [N_Axis]
  Reversed = true
  Type = 0
  expr: Length = <<Sketch>>.Constraints.Strength
FEATURE [Sketcher::SketchObject] Sketch002
  ExternalGeometry = -> [Pad001]
  FullyConstrained = true
  MapMode = 5
  Placement = pos=(3.7,16.5,-29.5) rot=(0.57735,-0.57735,-0.57735;2.0944rad)
  Support = -> [Pad001]
  sketch-geometry (4):
    g0: LineSegment StartX=-9.45 StartY=9.5 StartZ=0 EndX=-7.45 EndY=9.5 EndZ=0
    g1: LineSegment StartX=-7.45 StartY=9.5 StartZ=0 EndX=-7.45 EndY=7.5 EndZ=0
    g2: LineSegment StartX=-7.45 StartY=7.5 StartZ=0 EndX=-9.45 EndY=7.5 EndZ=0
    g3: LineSegment StartX=-9.45 StartY=7.5 StartZ=0 EndX=-9.45 EndY=9.5 EndZ=0
  constraints (11):
    c: Coincident(g0,g1)
    c: Coincident(g1,g2)
    c: Coincident(g2,g3)
    c: Coincident(g3,g0)
    c: Horizontal(g0)
    c: Horizontal(g2)
    c: Vertical(g1)
    c: Vertical(g3)
    c: DistanceX(g2,g2) = 2
    c: Coincident(g0,g-3)
    c: DistanceY(g1,g1) = 2
FEATURE [PartDesign::Pad] Pad002
  BaseFeature = -> Pad001
  Direction = (-1,-4e-16,0)
  Length = 13
  Length2 = 10
  Placement = pos=(-16.5,16.5,-29.5) rot=(0,0,-1;1.5708rad)
  Profile = -> Sketch002
  ReferenceAxis = -> Sketch002 [N_Axis]
  Reversed = true
  Type = 0
  expr: Length = <<Pad001>>.Length + <<Datasheet>>#<<mgn9c>>.Dim_H - <<Datasheet>>#<<mgn9c>>.Dim_H1
FEATURE [Sketcher::SketchObject] Sketch003
  ExternalGeometry = -> [Pad002]
  FullyConstrained = true
  MapMode = 5
  Placement = pos=(16.7,16.5,-29.5) rot=(0.57735,0.57735,0.57735;2.0944rad)
  Support = -> [Pad002]
  expr: Constraints[17] = <<NormalConnectorMagnet>>#<<Sketch002>>.Constraints.SlideToMagnetCenter
  sketch-geometry (13):
    g0: LineSegment StartX=9.45 StartY=9.5 StartZ=0 EndX=4.45 EndY=9.5 EndZ=0
    g1: LineSegment StartX=4.45 StartY=9.5 StartZ=0 EndX=4.45 EndY=2.35 EndZ=0
    g2: LineSegment StartX=4.45 StartY=2.35 StartZ=0 EndX=9.45 EndY=2.35 EndZ=0
    g3: LineSegment StartX=9.45 StartY=2.35 StartZ=0 EndX=9.45 EndY=9.5 EndZ=0
    g4: Circle CenterX=6.95 CenterY=4.85 CenterZ=0 NormalX=0 NormalY=0 NormalZ=1 AngleXU=0 Radius=1.5
    g5: GeomPoint X=8.45 Y=4.85 Z=0
    g6: GeomPoint X=6.95 Y=3.35 Z=0
    g7: LineSegment StartX=6.95 StartY=3.35 StartZ=0 EndX=6.95 EndY=2.35 EndZ=0
    g8: LineSegment StartX=7.45 StartY=7.5 StartZ=0 EndX=4.45 EndY=6.35 EndZ=0
    g9: LineSegment StartX=4.45 StartY=6.35 StartZ=0 EndX=4.45 EndY=2.35 EndZ=0
    g10: GeomPoint X=6.95 Y=6.35 Z=0
    g11: LineSegment StartX=7.45 StartY=9.5 StartZ=0 EndX=9.45 EndY=9.5 EndZ=0
    g12: LineSegment StartX=7.45 StartY=7.5 StartZ=0 EndX=7.45 EndY=9.5 EndZ=0
  constraints (32):
    c: Coincident(g0,g1)
    c: Coincident(g1,g2)
    c: Coincident(g2,g3)
    c: Coincident(g3,g0)
    c: Horizontal(g0)
    c: Horizontal(g2)
    c: Vertical(g1)
    c: Vertical(g3)
    c: PointOnObject(g-3,g3)
    c: PointOnObject(g-4,g0)
    c: Diameter(g4) = 3
    c: PointOnObject(g5,g4)
    c: DistanceX(g5,g0) = 1
    c: PointOnObject(g6,g4)
    c: DistanceY(g2,g6) = 1
    c: Horizontal(g5,g4)
    c: Vertical(g4,g6)
    c: DistanceY(g4,g0) = 4.65
    c: Coincident(g7,g6)
    c: Vertical(g7)
    c: Symmetric(g1,g2,g7)
    c: Coincident(g8,g-4)
    c: PointOnObject(g8,g1)
    c: Coincident(g9,g8)
    c: Coincident(g9,g2)
    c: PointOnObject(g10,g4)
    c: Vertical(g10,g4)
    c: Horizontal(g8,g10)
    c: Coincident(g12,g11)
    c: Coincident(g11,g-4)
    c: Coincident(g0,g11)
    c: Coincident(g8,g12)
FEATURE [PartDesign::Pad] Pad003
  BaseFeature = -> Pad002
  Direction = (1,4e-16,0)
  Length = 2
  Length2 = 10
  Placement = pos=(-16.5,16.5,-29.5) rot=(0,0,-1;1.5708rad)
  Profile = -> Sketch003
  ReferenceAxis = -> Sketch003 [N_Axis]
  Reversed = true
  Type = 0
  expr: Length = <<NormalConnectorMagnet>>#<<Pad002>>.Length
FEATURE [Sketcher::SketchObject] Sketch004
  ExternalGeometry = -> [Pad003]
  FullyConstrained = true
  MapMode = 5
  Placement = pos=(14.7,16.5,-29.5) rot=(0.57735,-0.57735,-0.57735;2.0944rad)
  Support = -> [Pad003]
  expr: Constraints[1] = <<NormalConnectorMagnet>>#<<Sketch003>>.Constraints.MagnetDiameter
  sketch-geometry (1):
    g0: Circle CenterX=-6.95 CenterY=4.85 CenterZ=0 NormalX=0 NormalY=0 NormalZ=1 AngleXU=0 Radius=2
  constraints (2):
    c: Coincident(g0,g-3)
    c: Diameter(g0) = 4
FEATURE [PartDesign::Pocket] Pocket
  BaseFeature = -> Pad003
  Direction = (1,0,0)
  Length = 1
  Length2 = 5
  Placement = pos=(-16.5,16.5,-29.5) rot=(0,0,-1;1.5708rad)
  Profile = -> Sketch004
  ReferenceAxis = -> Sketch004 [N_Axis]
  Type = 0
FEATURE [Sketcher::SketchObject] Sketch005
  ExternalGeometry = -> [Pocket]
  FullyConstrained = true
  MapMode = 5
  Placement = pos=(3.7,16.5,-29.5) rot=(0.57735,-0.57735,-0.57735;2.0944rad)
  Support = -> [Pocket]
  expr: Constraints[1] = <<Datasheet>>#<<mgn9c>>.Dim_D
  expr: Constraints[5] = <<Datasheet>>#<<mgn9c>>.Dim_D
  expr: Constraints[6] = <<Datasheet>>#<<mgn9c>>.Dim_D
  expr: Constraints[7] = <<Datasheet>>#<<mgn9c>>.Dim_D
  sketch-geometry (14):
    g0: Circle CenterX=-5 CenterY=27 CenterZ=0 NormalX=0 NormalY=0 NormalZ=1 AngleXU=0 Radius=3
    g1: Circle CenterX=5 CenterY=27 CenterZ=0 NormalX=0 NormalY=0 NormalZ=1 AngleXU=0 Radius=3
    g2: Circle CenterX=5 CenterY=12 CenterZ=0 NormalX=0 NormalY=0 NormalZ=1 AngleXU=0 Radius=3
    g3: Circle CenterX=-5 CenterY=12 CenterZ=0 NormalX=0 NormalY=0 NormalZ=1 AngleXU=0 Radius=3
    g4: ArcOfCircle CenterX=-5 CenterY=12 CenterZ=0 NormalX=0 NormalY=0 NormalZ=1 AngleXU=0 Radius=3 StartAngle=2.26252e-07 EndAngle=3.14159
    g5: ArcOfCircle CenterX=5 CenterY=12 CenterZ=0 NormalX=0 NormalY=0 NormalZ=1 AngleXU=0 Radius=3 StartAngle=6.28318 EndAngle=9.42479
    g6: LineSegment StartX=2 StartY=9.5 StartZ=0 EndX=8 EndY=9.5 EndZ=0
    g7: LineSegment StartX=8 StartY=9.5 StartZ=0 EndX=8 EndY=12 EndZ=0
    g8: LineSegment StartX=8 StartY=12 StartZ=0 EndX=2 EndY=12 EndZ=0
    g9: LineSegment StartX=2 StartY=12 StartZ=0 EndX=2 EndY=9.5 EndZ=0
    g10: LineSegment StartX=-2 StartY=7.5 StartZ=0 EndX=-8 EndY=7.5 EndZ=0
    g11: LineSegment StartX=-8 StartY=7.5 StartZ=0 EndX=-8 EndY=12 EndZ=0
    g12: LineSegment StartX=-8 StartY=12 StartZ=0 EndX=-2 EndY=12 EndZ=0
    g13: LineSegment StartX=-2 StartY=12 StartZ=0 EndX=-2 EndY=7.5 EndZ=0
  constraints (36):
    c: Coincident(g0,g-3)
    c: Diameter(g0) = 6
    c: Coincident(g1,g-4)
    c: Coincident(g2,g-5)
    c: Coincident(g3,g-6)
    c: Diameter(g1) = 6
    c: Diameter(g2) = 6
    c: Diameter(g3) = 6
    c: Coincident(g4,g3)
    c: PointOnObject(g4,g3)
    c: Coincident(g5,g2)
    c: PointOnObject(g5,g2)
    c: Coincident(g6,g7)
    c: Coincident(g7,g8)
    c: Coincident(g8,g9)
    c: Coincident(g9,g6)
    c: Horizontal(g6)
    c: Horizontal(g8)
    c: Vertical(g7)
    c: Vertical(g9)
    c: Coincident(g7,g5)
    c: PointOnObject(g6,g-7)
    c: Coincident(g5,g8)
    c: Coincident(g10,g11)
    c: Coincident(g11,g12)
    c: Coincident(g12,g13)
    c: Coincident(g13,g10)
    c: Horizontal(g10)
    c: Horizontal(g12)
    c: Vertical(g11)
    c: Vertical(g13)
    c: Coincident(g11,g4)
    c: Coincident(g4,g12)
    c: Tangent(g13,g4)
    c: Tangent(g9,g5)
    c: PointOnObject(g-8,g10)
FEATURE [PartDesign::Pocket] Pocket001
  BaseFeature = -> Pocket
  Direction = (1,9e-16,0)
  Length = 3
  Length2 = 5
  Placement = pos=(-16.5,16.5,-29.5) rot=(0,0,-1;1.5708rad)
  Profile = -> Sketch005
  ReferenceAxis = -> Sketch005 [N_Axis]
  Type = 4
  expr: Length = <<Pad001>>.Length - 2 mm
FEATURE [PartDesign::Body] Body  label="JoystickHolder"
  Group = -> [Binder,Binder001,Sketch,Pad,Sketch001,Pad001,Sketch002,Pad002,Sketch003,Pad003,Sketch004,Pocket,Sketch005,Pocket001]
  Origin = -> Origin
  Placement = pos=(0,0,-4) rot=(0,0,1;0rad)
  Tip = -> Pocket001
COMPONENT P23 — recipe-attached ("Revolution", a linked part whose construction recipe lives in a companion FreeCAD document of the same project; that document's serialized recipe follows).
Construction recipe (the companion document, serialized — sketch geometry with constraints, then the solid features built on it; lengths are millimeters unless a unit is written):

FCSTD DOCUMENT  (FreeCAD 0.21R33668 +26 (Git))
Label: R202
License: All rights reserved
LicenseURL: http://en.wikipedia.org/wiki/All_rights_reserved
objects: Sketcher::SketchObject×2, PartDesign::Pad×1, PartDesign::Revolution×1, Spreadsheet::Sheet×1
note: 6 computed .brp shape members not serialized (recipe doc carries the construction recipe); baked Part::Feature solids carry a one-line shape summary decoded from their .brp

FEATURE [Sketcher::SketchObject] Sketch003
  AttachmentOffset = pos=(0,0,0) rot=(0,0,1;1.5708rad)
  FullyConstrained = true
  MapMode = 5
  Placement = pos=(0,0,0) rot=(0,0,1;1.5708rad)
  Support = -> [XY_Plane003]
  expr: .Constraints.ScrewDistance = <<Joystick>>.SD
  expr: Constraints[10] = <<Joystick>>.BW
  expr: Constraints[25] = <<Joystick>>.BW * 0.5
  expr: Constraints[26] = <<Joystick>>.PE
  expr: Constraints[27] = <<Joystick>>.BD * 0.5
  expr: Constraints[28] = <<Joystick>>.PE
  expr: Constraints[50] = <<Joystick>>.SD
  expr: Constraints[53] = <<Joystick>>.SBD / 2
  expr: Constraints[54] = <<Joystick>>.SBD / 2
  expr: Constraints[55] = <<Joystick>>.SBD / 2
  expr: Constraints[56] = <<Joystick>>.SBD / 2
  expr: Constraints[9] = <<Joystick>>.BD
  sketch-geometry (23):
    g0: LineSegment StartX=-20.2 StartY=20.2 StartZ=0 EndX=20.2 EndY=20.2 EndZ=0
    g1: LineSegment StartX=20.2 StartY=20.2 StartZ=0 EndX=20.2 EndY=-20.2 EndZ=0
    g2: LineSegment StartX=20.2 StartY=-20.2 StartZ=0 EndX=-20.2 EndY=-20.2 EndZ=0
    g3: LineSegment StartX=-20.2 StartY=-20.2 StartZ=0 EndX=-20.2 EndY=20.2 EndZ=0
    g4: LineSegment StartX=-10.1 StartY=29.4 StartZ=0 EndX=10.1 EndY=29.4 EndZ=0
    g5: LineSegment StartX=10.1 StartY=29.4 StartZ=0 EndX=10.1 EndY=20.2 EndZ=0
    g6: LineSegment StartX=-10.1 StartY=20.2 StartZ=0 EndX=-10.1 EndY=29.4 EndZ=0
    g7: LineSegment StartX=-29.4 StartY=10.1 StartZ=0 EndX=-20.2 EndY=10.1 EndZ=0
    g8: LineSegment StartX=-20.2 StartY=-10.1 StartZ=0 EndX=-29.4 EndY=-10.1 EndZ=0
    g9: LineSegment StartX=-29.4 StartY=-10.1 StartZ=0 EndX=-29.4 EndY=10.1 EndZ=0
    g10: GeomPoint X=-20.2 Y=-2e-16 Z=0
    g11: LineSegment StartX=-20.2 StartY=20.2 StartZ=0 EndX=-20.2 EndY=10.1 EndZ=0
    g12: LineSegment StartX=-20.2 StartY=20.2 StartZ=0 EndX=-10.1 EndY=20.2 EndZ=0
    g13: LineSegment StartX=-20.2 StartY=-20.2 StartZ=0 EndX=-20.2 EndY=-10.1 EndZ=0
    g14: LineSegment StartX=10.1 StartY=20.2 StartZ=0 EndX=20.2 EndY=20.2 EndZ=0
    g15: Circle CenterX=-16.25 CenterY=16.25 CenterZ=0 NormalX=0 NormalY=0 NormalZ=1 AngleXU=0 Radius=1
    g16: Circle CenterX=16.25 CenterY=16.25 CenterZ=0 NormalX=0 NormalY=0 NormalZ=1 AngleXU=0 Radius=1
    g17: Circle CenterX=16.25 CenterY=-16.25 CenterZ=0 NormalX=0 NormalY=0 NormalZ=1 AngleXU=0 Radius=1
    g18: Circle CenterX=-16.25 CenterY=-16.25 CenterZ=0 NormalX=0 NormalY=0 NormalZ=1 AngleXU=0 Radius=1
    g19: LineSegment StartX=-16.25 StartY=16.25 StartZ=0 EndX=16.25 EndY=16.25 EndZ=0
    g20: LineSegment StartX=16.25 StartY=16.25 StartZ=0 EndX=16.25 EndY=-16.25 EndZ=0
    g21: LineSegment StartX=16.25 StartY=-16.25 StartZ=0 EndX=-16.25 EndY=-16.25 EndZ=0
    g22: LineSegment StartX=-16.25 StartY=-16.25 StartZ=0 EndX=-16.25 EndY=16.25 EndZ=0
  constraints (57):
    c: Coincident(g0,g1)
    c: Coincident(g1,g2)
    c: Coincident(g2,g3)
    c: Coincident(g3,g0)
    c: Horizontal(g0)
    c: Horizontal(g2)
    c: Vertical(g1)
    c: Vertical(g3)
    c: Symmetric(g2,g0,g-1)
    c: DistanceY(g1,g1) = 40.4
    c: DistanceX(g0,g0) = 40.4
    c: Coincident(g4,g5)
    c: Coincident(g6,g4)
    c: Horizontal(g4)
    c: Vertical(g5)
    c: Vertical(g6)
    c: PointOnObject(g5,g0)
    c: Coincident(g8,g9)
    c: Coincident(g9,g7)
    c: Horizontal(g7)
    c: Horizontal(g8)
    c: Vertical(g9)
    c: Symmetric(g0,g2,g10)
    c: Symmetric(g7,g8,g10)
    c: Symmetric(g6,g5,g-2)
    c: DistanceX(g4,g4) = 20.2
    c: DistanceY(g5,g5) = 9.2
    c: DistanceY(g9,g9) = 20.2
    c: DistanceX(g7,g7) = 9.2
    c: Coincident(g11,g0)
    c: Coincident(g11,g7)
    c: Coincident(g12,g11)
    c: Coincident(g13,g2)
    c: Coincident(g13,g8)
    c: Vertical(g13)
    c: Coincident(g12,g6)
    c: Coincident(g14,g5)
    c: Coincident(g14,g1)
    c: Coincident(g19,g20)
    c: Coincident(g20,g21)
    c: Coincident(g21,g22)
    c: Coincident(g22,g19)
    c: Horizontal(g19)
    c: Horizontal(g21)
    c: Vertical(g20)
    c: Vertical(g22)
    c: Coincident(g19,g15)
    c: Coincident(g20,g17)
    c: Coincident(g16,g19)
    c: Coincident(g18,g21)
    c: DistanceY(g22,g22) = 32.5
    c: DistanceX(g19,g19) = 32.5  'ScrewDistance'
    c: Symmetric(g16,g18,g-1)
    c: Radius(g18) = 1
    c: Radius(g15) = 1
    c: Radius(g16) = 1
    c: Radius(g17) = 1
FEATURE [PartDesign::Pad] Pad001
  Direction = (0,0,1)
  Length = 25.5
  Length2 = 100
  Profile = -> Sketch003
  Type = 0
  expr: Length = <<Joystick>>.BH
FEATURE [Sketcher::SketchObject] Sketch004
  FullyConstrained = true
  MapMode = 5
  Placement = pos=(0,0,0) rot=(1,0,0;1.5708rad)
  Support = -> [XZ_Plane003]
  expr: .AttachmentOffset.Rotation.Angle = <<Joystick>>.DEMO_ANGLE
  expr: .AttachmentOffset.Rotation.Axis.x = <<Joystick>>.DEMO_ANGLE_X
  expr: .AttachmentOffset.Rotation.Axis.z = <<Joystick>>.DEMO_ANGLE_Z
  expr: Constraints[10] = <<Joystick>>.B2JT
  expr: Constraints[11] = <<Joystick>>.JHH
  expr: Constraints[12] = <<Joystick>>.JD / 2
  expr: Constraints[13] = <<Joystick>>.BH / 2
  expr: Constraints[15] = <<Joystick>>.JD / 6
  sketch-geometry (7):
    g0: LineSegment StartX=0 StartY=84 StartZ=0 EndX=12.31 EndY=84 EndZ=0
    g1: LineSegment StartX=12.31 StartY=84 StartZ=0 EndX=17.5 EndY=75.9 EndZ=0
    g2: LineSegment StartX=17.5 StartY=75.9 StartZ=0 EndX=17.5 EndY=59.3 EndZ=0
    g3: LineSegment StartX=17.5 StartY=59.3 StartZ=0 EndX=5.83333 EndY=44.5 EndZ=0
    g4: LineSegment StartX=5.83333 StartY=44.5 StartZ=0 EndX=5.83333 EndY=12.75 EndZ=0
    g5: LineSegment StartX=5.83333 StartY=12.75 StartZ=0 EndX=0 EndY=12.75 EndZ=0
    g6: LineSegment StartX=0 StartY=84 StartZ=0 EndX=0 EndY=12.75 EndZ=0
  constraints (21):
    c: PointOnObject(g0,g-2)
    c: Coincident(g1,g0)
    c: Coincident(g2,g1)
    c: Vertical(g2)
    c: Coincident(g3,g2)
    c: Coincident(g4,g3)
    c: Coincident(g5,g4)
    c: PointOnObject(g5,g-2)
    c: Horizontal(g5)
    c: Horizontal(g0)
    c: DistanceY(g0) = 84
    c: DistanceY(g3,g0) = 39.5
    c: DistanceX(g1) = 17.5
    c: DistanceY(g5) = 12.75
    c: Vertical(g4)
    c: DistanceX(g5,g5) = 5.83333
    c: DistanceY(g1) = 75.9
    c: DistanceY(g2) = 59.3
    c: DistanceX(g0) = 12.31
    c: Coincident(g6,g0)
    c: Coincident(g6,g5)
FEATURE [PartDesign::Revolution] Revolution
  Angle = 360
  Axis = (0,-2e-16,1)
  Base = (0,0,0)
  BaseFeature = -> Pad001
  Profile = -> Sketch004
  ReferenceAxis = -> Sketch004 [V_Axis]
  Reversed = true
FEATURE [Spreadsheet::Sheet] Spreadsheet005  label="Joystick"
  cells = A2='Demo Angles; A3='X; B3(DEMO_ANGLE_X)=0; A4='Y; B4(DEMO_ANGLE_Y)=1; A5='Z; B5(DEMO_ANGLE_Z)=0; A6='Angle; B6(DEMO_ANGLE)=0; A7='Screw Distance; B7(SD)=32.5; A9='Screw; B9='M2x12; A10='Screw Body Diameter; B10(SBD)=2; A11='Base Depth; B11(BD)=40.4; A12='Base Width; B12(BW)=40.4; A13='Base Height; B13(BH)=25.5; A14='Potentiometer Extrusion; B14(PE)==49.6 - 40.4; A15='Potentiometer Extrusion Depth; B15(PED)==BD + PE; A16='Potentiometer Extrusion Width; B16(PEW)==BD + 2 * PE; A18='Joystick Handle Height; B18(JHH)=39.5; A19='Joystick Diameter; B19(JD)=35; A22='Base to Joystick Top; B22(B2JT)=84
PROVENANCE & LICENSES
A FreeCAD (.FCStd) document from a public repository crawl; recipes are the document's own serialized feature recipes (and, for linked parts, companion documents' recipes).
License: as declared in the source repository (recorded in the dataset sidecar).
